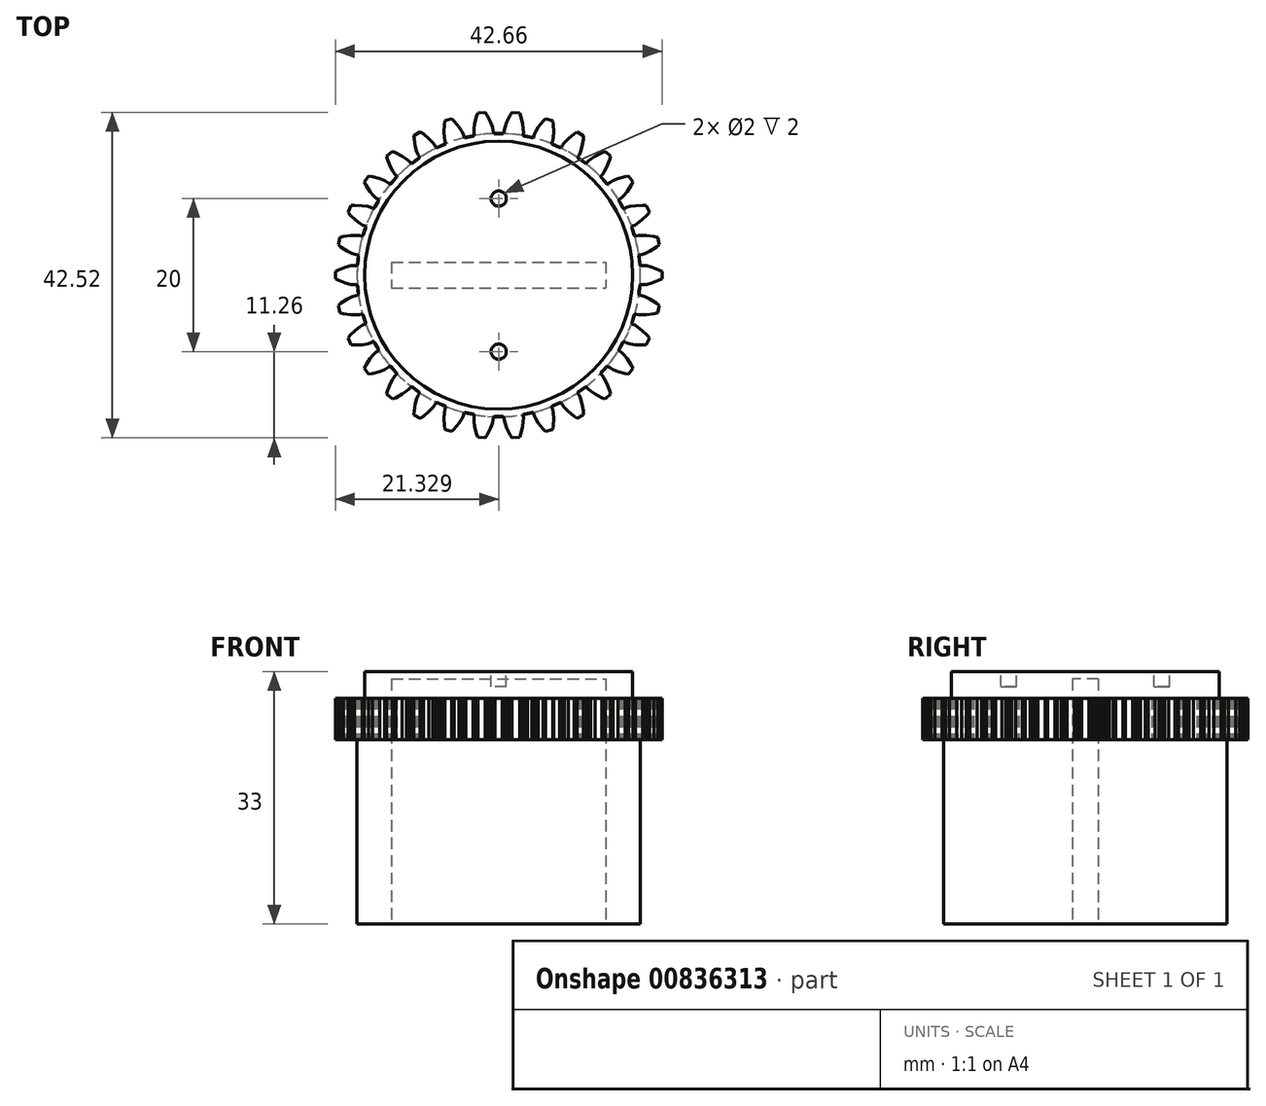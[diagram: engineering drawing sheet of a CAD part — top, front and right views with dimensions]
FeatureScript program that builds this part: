
annotation { "Feature Type Name" : "Feature", "Feature Type Description" : "" }
export const myFeature = defineFeature(function(context is Context, id is Id, definition is map)
    precondition{}
    {
        {
            var Q0;
            Q0=qCreatedBy(makeId("Top.planeOp"),FACE);
            var sketch = newSketch(context, id + "F0", { "sketchPlane" : qUnion([Q0])});
            skLineSegment(sketch, "E0", {"start": v(5.95, 16.64) * mm, "end": v(6.04, 16.7) * mm});
            skLineSegment(sketch, "E1", {"start": v(6.04, 16.7) * mm, "end": v(6.12, 16.74) * mm});
            skLineSegment(sketch, "E2", {"start": v(21.02, -17.09) * mm, "end": v(21.05, -17.07) * mm});
            skLineSegment(sketch, "E3", {"start": v(32.31, -2.53) * mm, "end": v(32.33, -2.41) * mm});
            skLineSegment(sketch, "E4", {"start": v(32.33, -2.41) * mm, "end": v(32.35, -2.32) * mm});
            skLineSegment(sketch, "E5", {"start": v(6.12, 16.74) * mm, "end": v(6.43, 16.86) * mm});
            skLineSegment(sketch, "E6", {"start": v(6.43, 16.86) * mm, "end": v(6.95, 17.06) * mm});
            skLineSegment(sketch, "E7", {"start": v(6.13, -16.74) * mm, "end": v(6.43, -16.86) * mm});
            skLineSegment(sketch, "E8", {"start": v(6.43, -16.86) * mm, "end": v(6.95, -17.06) * mm});
            skLineSegment(sketch, "E9", {"start": v(17.47, -18.17) * mm, "end": v(17.79, -18.09) * mm});
            skLineSegment(sketch, "E10", {"start": v(17.79, -18.09) * mm, "end": v(18.32, -17.95) * mm});
            skLineSegment(sketch, "E11", {"start": v(21.86, -16.75) * mm, "end": v(21.96, -16.7) * mm});
            skLineSegment(sketch, "E12", {"start": v(21.96, -16.7) * mm, "end": v(22.05, -16.64) * mm});
            skLineSegment(sketch, "E13", {"start": v(10.18, 18.1) * mm, "end": v(10.52, 18.17) * mm});
            skLineSegment(sketch, "E14", {"start": v(-4.35, 2.32) * mm, "end": v(-4.34, 2.41) * mm});
            skLineSegment(sketch, "E15", {"start": v(-4.34, 2.41) * mm, "end": v(-4.31, 2.53) * mm});
            skLineSegment(sketch, "E16", {"start": v(10.53, -18.17) * mm, "end": v(10.63, -18.18) * mm});
            skLineSegment(sketch, "E17", {"start": v(10.63, -18.18) * mm, "end": v(10.73, -18.2) * mm});
            skLineSegment(sketch, "E18", {"start": v(32.37, 1.98) * mm, "end": v(32.35, 2.27) * mm});
            skLineSegment(sketch, "E19", {"start": v(10.18, -18.1) * mm, "end": v(10.53, -18.17) * mm});
            skLineSegment(sketch, "E20", {"start": v(27.49, -12.66) * mm, "end": v(27.7, -12.4) * mm});
            skLineSegment(sketch, "E21", {"start": v(27.7, -12.4) * mm, "end": v(28.05, -11.98) * mm});
            skLineSegment(sketch, "E22", {"start": v(21.02, 17.09) * mm, "end": v(21.05, 17.07) * mm});
            skLineSegment(sketch, "E23", {"start": v(32.35, -2.27) * mm, "end": v(32.37, -1.98) * mm});
            skLineSegment(sketch, "E24", {"start": v(32.33, 2.41) * mm, "end": v(32.31, 2.52) * mm});
            skLineSegment(sketch, "E25", {"start": v(17.26, 18.2) * mm, "end": v(17.37, 18.18) * mm});
            skLineSegment(sketch, "E26", {"start": v(17.47, 18.17) * mm, "end": v(17.79, 18.09) * mm});
            skLineSegment(sketch, "E27", {"start": v(17.79, 18.09) * mm, "end": v(18.32, 17.95) * mm});
            skLineSegment(sketch, "E28", {"start": v(19.8, -20.1) * mm, "end": v(20.12, -20.44) * mm});
            skLineSegment(sketch, "E29", {"start": v(22.35, -17) * mm, "end": v(22.6, -17.33) * mm});
            skLineSegment(sketch, "E30", {"start": v(28.5, -15.07) * mm, "end": v(28.64, -15.52) * mm});
            skLineSegment(sketch, "E31", {"start": v(5.65, -17) * mm, "end": v(5.77, -16.76) * mm});
            skLineSegment(sketch, "E32", {"start": v(27.4, -13) * mm, "end": v(27.58, -13.2) * mm});
            skLineSegment(sketch, "E33", {"start": v(17.23, 18.66) * mm, "end": v(17.22, 19.08) * mm});
            skLineSegment(sketch, "E34", {"start": v(28.64, -15.52) * mm, "end": v(27.9, -16.18) * mm});
            skLineSegment(sketch, "E35", {"start": v(27.34, -12.9) * mm, "end": v(27.4, -13) * mm});
            skLineSegment(sketch, "E36", {"start": v(27.47, -16) * mm, "end": v(26.6, -15.55) * mm});
            skLineSegment(sketch, "E37", {"start": v(26.02, -15.16) * mm, "end": v(25.7, -14.88) * mm});
            skLineSegment(sketch, "E38", {"start": v(10.8, -18.28) * mm, "end": v(10.8, -18.4) * mm});
            skLineSegment(sketch, "E39", {"start": v(27.9, -16.18) * mm, "end": v(27.47, -16) * mm});
            skLineSegment(sketch, "E40", {"start": v(26.6, -15.55) * mm, "end": v(26.02, -15.16) * mm});
            skLineSegment(sketch, "E41", {"start": v(10.73, -18.2) * mm, "end": v(10.8, -18.28) * mm});
            skLineSegment(sketch, "E42", {"start": v(10.73, -18.2) * mm, "end": v(10.63, -18.15) * mm});
            skLineSegment(sketch, "E43", {"start": v(13.41, -18.48) * mm, "end": v(13.33, -18.55) * mm});
            skLineSegment(sketch, "E44", {"start": v(30.5, -8.72) * mm, "end": v(30.4, -8.7) * mm});
            skLineSegment(sketch, "E45", {"start": v(18.56, -18.1) * mm, "end": v(18.64, -18.36) * mm});
            skLineSegment(sketch, "E46", {"start": v(24.7, -16.12) * mm, "end": v(24.9, -16.8) * mm});
            skLineSegment(sketch, "E47", {"start": v(-5.77, -3.14) * mm, "end": v(-5.14, -2.83) * mm});
            skLineSegment(sketch, "E48", {"start": v(34.3, -5.02) * mm, "end": v(33.33, -5.17) * mm});
            skLineSegment(sketch, "E49", {"start": v(12.95, 19.99) * mm, "end": v(13.18, 19.33) * mm});
            skLineSegment(sketch, "E50", {"start": v(12.26, 21.26) * mm, "end": v(12.5, 20.86) * mm});
            skLineSegment(sketch, "E51", {"start": v(12.5, 20.86) * mm, "end": v(12.95, 19.99) * mm});
            skLineSegment(sketch, "E52", {"start": v(33.33, -5.17) * mm, "end": v(32.63, -5.2) * mm});
            skLineSegment(sketch, "E53", {"start": v(32.63, -5.2) * mm, "end": v(32.22, -5.16) * mm});
            skLineSegment(sketch, "E54", {"start": v(28.9, -12.33) * mm, "end": v(28.54, -12.12) * mm});
            skLineSegment(sketch, "E55", {"start": v(13.28, 18.92) * mm, "end": v(13.18, 19.33) * mm});
            skLineSegment(sketch, "E56", {"start": v(0.6, -12.7) * mm, "end": v(0.66, -12.8) * mm});
            skLineSegment(sketch, "E57", {"start": v(15.5, -20.86) * mm, "end": v(15.74, -21.26) * mm});
            skLineSegment(sketch, "E58", {"start": v(16.72, -21.16) * mm, "end": v(15.74, -21.26) * mm});
            skLineSegment(sketch, "E59", {"start": v(15.05, -19.99) * mm, "end": v(15.5, -20.86) * mm});
            skLineSegment(sketch, "E60", {"start": v(28.33, -11.96) * mm, "end": v(28.23, -11.92) * mm});
            skLineSegment(sketch, "E61", {"start": v(27.82, 13.54) * mm, "end": v(27.58, 13.2) * mm});
            skLineSegment(sketch, "E62", {"start": v(28.54, -12.12) * mm, "end": v(28.33, -11.96) * mm});
            skLineSegment(sketch, "E63", {"start": v(9.44, 18.1) * mm, "end": v(9.36, 18.36) * mm});
            skLineSegment(sketch, "E64", {"start": v(10.78, 19.08) * mm, "end": v(10.77, 18.66) * mm});
            skLineSegment(sketch, "E65", {"start": v(10.8, -18.4) * mm, "end": v(10.77, -18.66) * mm});
            skLineSegment(sketch, "E66", {"start": v(-4.3, -2.4) * mm, "end": v(-4.31, -2.52) * mm});
            skLineSegment(sketch, "E67", {"start": v(17.47, -18.17) * mm, "end": v(17.26, -18.2) * mm});
            skLineSegment(sketch, "E68", {"start": v(-4.36, -2.32) * mm, "end": v(-4.31, -2.52) * mm});
            skLineSegment(sketch, "E69", {"start": v(21.86, 16.75) * mm, "end": v(22.05, 16.64) * mm});
            skLineSegment(sketch, "E70", {"start": v(-4.36, -2.32) * mm, "end": v(-4.44, -1.35) * mm});
            skLineSegment(sketch, "E71", {"start": v(0.51, -12.66) * mm, "end": v(-0.12, -11.93) * mm});
            skLineSegment(sketch, "E72", {"start": v(30.21, -8.91) * mm, "end": v(29.7, -9.75) * mm});
            skLineSegment(sketch, "E73", {"start": v(30.5, 1.75) * mm, "end": v(30.5, -1.75) * mm, "construction": true});
            skLineSegment(sketch, "E74", {"start": v(27.48, 12.66) * mm, "end": v(27.34, 12.8) * mm});
            skLineSegment(sketch, "E75", {"start": v(0.51, 12.66) * mm, "end": v(0.66, 12.8) * mm});
            skLineSegment(sketch, "E76", {"start": v(27.49, -12.66) * mm, "end": v(27.34, -12.8) * mm});
            skLineSegment(sketch, "E77", {"start": v(-2.5, -1.75) * mm, "end": v(-2.5, 1.75) * mm, "construction": true});
            skLineSegment(sketch, "E78", {"start": v(-2.21, 8.9) * mm, "end": v(-1.7, 9.75) * mm});
            skLineSegment(sketch, "E79", {"start": v(0.51, -12.66) * mm, "end": v(0.66, -12.8) * mm});
            skLineSegment(sketch, "E80", {"start": v(30.21, 8.9) * mm, "end": v(29.74, 9.64) * mm});
            skLineSegment(sketch, "E81", {"start": v(30.21, -8.91) * mm, "end": v(30.3, -8.73) * mm});
            skLineSegment(sketch, "E82", {"start": v(10.52, 18.17) * mm, "end": v(10.73, 18.2) * mm});
            skLineSegment(sketch, "E83", {"start": v(17.23, -18.66) * mm, "end": v(17.2, -18.4) * mm});
            skLineSegment(sketch, "E84", {"start": v(-3.54, -12.14) * mm, "end": v(-3.32, -11.73) * mm});
            skLineSegment(sketch, "E85", {"start": v(30.4, 8.7) * mm, "end": v(30.5, 8.72) * mm});
            skLineSegment(sketch, "E86", {"start": v(-2.97, -12.93) * mm, "end": v(-3.54, -12.14) * mm});
            skLineSegment(sketch, "E87", {"start": v(-5.68, 8.23) * mm, "end": v(-5.38, 7.87) * mm});
            skLineSegment(sketch, "E88", {"start": v(21.12, 19.67) * mm, "end": v(21.17, 18.69) * mm});
            skLineSegment(sketch, "E89", {"start": v(9.36, 18.36) * mm, "end": v(9.18, 18.74) * mm});
            skLineSegment(sketch, "E90", {"start": v(-4.69, 7.18) * mm, "end": v(-5.38, 7.87) * mm});
            skLineSegment(sketch, "E91", {"start": v(31.85, 5.1) * mm, "end": v(31.96, 5.1) * mm});
            skLineSegment(sketch, "E92", {"start": v(-2.97, 12.93) * mm, "end": v(-2.5, 12.85) * mm});
            skLineSegment(sketch, "E93", {"start": v(28.23, -11.92) * mm, "end": v(28.12, -11.93) * mm});
            skLineSegment(sketch, "E94", {"start": v(34.6, 3.67) * mm, "end": v(33.77, 3.14) * mm});
            skLineSegment(sketch, "E95", {"start": v(31.39, -6.27) * mm, "end": v(31.43, -6.37) * mm});
            skLineSegment(sketch, "E96", {"start": v(12.95, -19.99) * mm, "end": v(12.5, -20.86) * mm});
            skLineSegment(sketch, "E97", {"start": v(10.63, 18.15) * mm, "end": v(10.73, 18.2) * mm});
            skLineSegment(sketch, "E98", {"start": v(3.3, 16.12) * mm, "end": v(3.46, 15.73) * mm});
            skLineSegment(sketch, "E99", {"start": v(21.12, 18) * mm, "end": v(21.04, 17.58) * mm});
            skLineSegment(sketch, "E100", {"start": v(34.96, 3.95) * mm, "end": v(34.6, 3.67) * mm});
            skLineSegment(sketch, "E101", {"start": v(-4.31, 2.53) * mm, "end": v(-4.3, 2.4) * mm});
            skLineSegment(sketch, "E102", {"start": v(20.95, -17.33) * mm, "end": v(20.93, -17.22) * mm});
            skLineSegment(sketch, "E103", {"start": v(24.4, -15.5) * mm, "end": v(24.36, -15.4) * mm});
            skLineSegment(sketch, "E104", {"start": v(9.36, -18.36) * mm, "end": v(9.44, -18.1) * mm});
            skLineSegment(sketch, "E105", {"start": v(13.28, -18.92) * mm, "end": v(13.3, -18.65) * mm});
            skLineSegment(sketch, "E106", {"start": v(17.2, -18.4) * mm, "end": v(17.2, -18.28) * mm});
            skLineSegment(sketch, "E107", {"start": v(27.39, 12.7) * mm, "end": v(27.34, 12.8) * mm});
            skLineSegment(sketch, "E108", {"start": v(5.65, 17) * mm, "end": v(5.4, 17.33) * mm});
            skLineSegment(sketch, "E109", {"start": v(17.2, 18.28) * mm, "end": v(17.2, 18.4) * mm});
            skLineSegment(sketch, "E110", {"start": v(10.7, 17.33) * mm, "end": v(8.55, 16.78) * mm});
            skLineSegment(sketch, "E111", {"start": v(17.3, 17.33) * mm, "end": v(15.1, 17.6) * mm});
            skLineSegment(sketch, "E112", {"start": v(8.55, 16.78) * mm, "end": v(6.49, 15.96) * mm});
            skLineSegment(sketch, "E113", {"start": v(15.1, 17.6) * mm, "end": v(12.9, 17.6) * mm});
            skLineSegment(sketch, "E114", {"start": v(19.45, 16.78) * mm, "end": v(17.3, 17.33) * mm});
            skLineSegment(sketch, "E115", {"start": v(12.9, 17.6) * mm, "end": v(10.7, 17.33) * mm});
            skLineSegment(sketch, "E116", {"start": v(23.1, 17.83) * mm, "end": v(22.6, 17.33) * mm});
            skLineSegment(sketch, "E117", {"start": v(20.93, 17.22) * mm, "end": v(20.95, 17.33) * mm});
            skLineSegment(sketch, "E118", {"start": v(30.5, 1.75) * mm, "end": v(-2.5, 1.75) * mm, "construction": true});
            skLineSegment(sketch, "E119", {"start": v(22.05, 16.64) * mm, "end": v(21.94, 16.66) * mm});
            skLineSegment(sketch, "E120", {"start": v(22.6, 17.33) * mm, "end": v(22.35, 17) * mm});
            skLineSegment(sketch, "E121", {"start": v(-2.5, -1.75) * mm, "end": v(30.5, -1.75) * mm, "construction": true});
            skLineSegment(sketch, "E122", {"start": v(21.94, 16.66) * mm, "end": v(21.05, 17.07) * mm});
            skLineSegment(sketch, "E123", {"start": v(22.15, 16.67) * mm, "end": v(22.05, 16.64) * mm});
            skLineSegment(sketch, "E124", {"start": v(22.22, 16.76) * mm, "end": v(22.15, 16.67) * mm});
            skLineSegment(sketch, "E125", {"start": v(22.35, 17) * mm, "end": v(22.22, 16.76) * mm});
            skLineSegment(sketch, "E126", {"start": v(20.98, 17.12) * mm, "end": v(20.93, 17.22) * mm});
            skLineSegment(sketch, "E127", {"start": v(23.85, 18.45) * mm, "end": v(23.1, 17.83) * mm});
            skLineSegment(sketch, "E128", {"start": v(24.24, 18.72) * mm, "end": v(23.85, 18.45) * mm});
            skLineSegment(sketch, "E129", {"start": v(26.02, 15.16) * mm, "end": v(25.7, 14.88) * mm});
            skLineSegment(sketch, "E130", {"start": v(26.6, 15.55) * mm, "end": v(26.02, 15.16) * mm});
            skLineSegment(sketch, "E131", {"start": v(24.38, 15.3) * mm, "end": v(24.36, 15.4) * mm});
            skLineSegment(sketch, "E132", {"start": v(25.05, 17.76) * mm, "end": v(25.09, 18.22) * mm});
            skLineSegment(sketch, "E133", {"start": v(24.54, 15.73) * mm, "end": v(24.7, 16.12) * mm});
            skLineSegment(sketch, "E134", {"start": v(24.36, 15.4) * mm, "end": v(24.4, 15.5) * mm});
            skLineSegment(sketch, "E135", {"start": v(24.4, 15.5) * mm, "end": v(24.54, 15.73) * mm});
            skLineSegment(sketch, "E136", {"start": v(24.9, 16.8) * mm, "end": v(25.05, 17.76) * mm});
            skLineSegment(sketch, "E137", {"start": v(25.23, 14.64) * mm, "end": v(24.46, 15.21) * mm});
            skLineSegment(sketch, "E138", {"start": v(25.09, 18.22) * mm, "end": v(24.24, 18.72) * mm});
            skLineSegment(sketch, "E139", {"start": v(24.7, 16.12) * mm, "end": v(24.9, 16.8) * mm});
            skLineSegment(sketch, "E140", {"start": v(25.44, 14.62) * mm, "end": v(25.33, 14.6) * mm});
            skLineSegment(sketch, "E141", {"start": v(25.53, 14.68) * mm, "end": v(25.44, 14.62) * mm});
            skLineSegment(sketch, "E142", {"start": v(25.7, 14.88) * mm, "end": v(25.53, 14.68) * mm});
            skLineSegment(sketch, "E143", {"start": v(-2.33, -10.37) * mm, "end": v(-2.78, -10.9) * mm});
            skLineSegment(sketch, "E144", {"start": v(21.12, 19.67) * mm, "end": v(21.06, 20.13) * mm});
            skLineSegment(sketch, "E145", {"start": v(-2.03, -10.08) * mm, "end": v(-2.33, -10.37) * mm});
            skLineSegment(sketch, "E146", {"start": v(20.95, 17.33) * mm, "end": v(21.04, 17.58) * mm});
            skLineSegment(sketch, "E147", {"start": v(3.64, -15.4) * mm, "end": v(3.6, -15.5) * mm});
            skLineSegment(sketch, "E148", {"start": v(13.18, -19.33) * mm, "end": v(13.28, -18.92) * mm});
            skLineSegment(sketch, "E149", {"start": v(27.47, 16) * mm, "end": v(26.6, 15.55) * mm});
            skLineSegment(sketch, "E150", {"start": v(6.95, -17.06) * mm, "end": v(7.02, -17.12) * mm});
            skLineSegment(sketch, "E151", {"start": v(32.68, -7.18) * mm, "end": v(32.13, -6.75) * mm});
            skLineSegment(sketch, "E152", {"start": v(19.8, 20.1) * mm, "end": v(19.19, 19.33) * mm});
            skLineSegment(sketch, "E153", {"start": v(20.12, 20.44) * mm, "end": v(19.8, 20.1) * mm});
            skLineSegment(sketch, "E154", {"start": v(32.13, -6.75) * mm, "end": v(31.77, -6.53) * mm});
            skLineSegment(sketch, "E155", {"start": v(21.06, 20.13) * mm, "end": v(20.12, 20.44) * mm});
            skLineSegment(sketch, "E156", {"start": v(21.12, 18) * mm, "end": v(21.17, 18.69) * mm});
            skLineSegment(sketch, "E157", {"start": v(13.3, -18.65) * mm, "end": v(13.33, -18.55) * mm});
            skLineSegment(sketch, "E158", {"start": v(21.94, -16.66) * mm, "end": v(22.05, -16.64) * mm});
            skLineSegment(sketch, "E159", {"start": v(-1.8, -9.93) * mm, "end": v(-2.03, -10.08) * mm});
            skLineSegment(sketch, "E160", {"start": v(18.64, 18.36) * mm, "end": v(18.56, 18.1) * mm});
            skLineSegment(sketch, "E161", {"start": v(22.05, -16.64) * mm, "end": v(22.15, -16.67) * mm});
            skLineSegment(sketch, "E162", {"start": v(18.82, 18.74) * mm, "end": v(18.64, 18.36) * mm});
            skLineSegment(sketch, "E163", {"start": v(7.02, -17.12) * mm, "end": v(7.06, -17.22) * mm});
            skLineSegment(sketch, "E164", {"start": v(17.36, 18.15) * mm, "end": v(17.26, 18.2) * mm});
            skLineSegment(sketch, "E165", {"start": v(17.2, -18.28) * mm, "end": v(17.26, -18.2) * mm});
            skLineSegment(sketch, "E166", {"start": v(19.19, 19.33) * mm, "end": v(18.82, 18.74) * mm});
            skLineSegment(sketch, "E167", {"start": v(18.42, 17.95) * mm, "end": v(18.32, 17.95) * mm});
            skLineSegment(sketch, "E168", {"start": v(18.5, 18) * mm, "end": v(18.42, 17.95) * mm});
            skLineSegment(sketch, "E169", {"start": v(18.56, 18.1) * mm, "end": v(18.5, 18) * mm});
            skLineSegment(sketch, "E170", {"start": v(22.15, -16.67) * mm, "end": v(22.22, -16.76) * mm});
            skLineSegment(sketch, "E171", {"start": v(33.38, -7.87) * mm, "end": v(32.68, -7.18) * mm});
            skLineSegment(sketch, "E172", {"start": v(17.26, 18.2) * mm, "end": v(17.2, 18.28) * mm});
            skLineSegment(sketch, "E173", {"start": v(21.05, -17.07) * mm, "end": v(21.94, -16.66) * mm});
            skLineSegment(sketch, "E174", {"start": v(21.04, -17.58) * mm, "end": v(20.95, -17.33) * mm});
            skLineSegment(sketch, "E175", {"start": v(21.17, -18.69) * mm, "end": v(21.12, -18) * mm});
            skLineSegment(sketch, "E176", {"start": v(17.2, 18.4) * mm, "end": v(17.23, 18.66) * mm});
            skLineSegment(sketch, "E177", {"start": v(20.93, -17.22) * mm, "end": v(20.98, -17.12) * mm});
            skLineSegment(sketch, "E178", {"start": v(14.48, 18.45) * mm, "end": v(13.52, 18.45) * mm});
            skLineSegment(sketch, "E179", {"start": v(14.7, 18.65) * mm, "end": v(14.67, 18.55) * mm});
            skLineSegment(sketch, "E180", {"start": v(14.72, 18.92) * mm, "end": v(14.7, 18.65) * mm});
            skLineSegment(sketch, "E181", {"start": v(14.81, 19.33) * mm, "end": v(14.72, 18.92) * mm});
            skLineSegment(sketch, "E182", {"start": v(15.05, 19.99) * mm, "end": v(14.81, 19.33) * mm});
            skLineSegment(sketch, "E183", {"start": v(21.12, -18) * mm, "end": v(21.04, -17.58) * mm});
            skLineSegment(sketch, "E184", {"start": v(14.67, 18.55) * mm, "end": v(14.59, 18.48) * mm});
            skLineSegment(sketch, "E185", {"start": v(25.09, -18.22) * mm, "end": v(25.05, -17.76) * mm});
            skLineSegment(sketch, "E186", {"start": v(16.87, 20.72) * mm, "end": v(16.72, 21.16) * mm});
            skLineSegment(sketch, "E187", {"start": v(13.3, 18.65) * mm, "end": v(13.28, 18.92) * mm});
            skLineSegment(sketch, "E188", {"start": v(31.75, -5.15) * mm, "end": v(31.85, -5.1) * mm});
            skLineSegment(sketch, "E189", {"start": v(11.12, 20.72) * mm, "end": v(10.87, 19.77) * mm});
            skLineSegment(sketch, "E190", {"start": v(12.26, 21.26) * mm, "end": v(11.28, 21.16) * mm});
            skLineSegment(sketch, "E191", {"start": v(10.87, 19.77) * mm, "end": v(10.78, 19.08) * mm});
            skLineSegment(sketch, "E192", {"start": v(33.68, -8.23) * mm, "end": v(33.38, -7.87) * mm});
            skLineSegment(sketch, "E193", {"start": v(15.74, 21.26) * mm, "end": v(15.5, 20.86) * mm});
            skLineSegment(sketch, "E194", {"start": v(17.12, 19.77) * mm, "end": v(16.87, 20.72) * mm});
            skLineSegment(sketch, "E195", {"start": v(11.28, 21.16) * mm, "end": v(11.12, 20.72) * mm});
            skLineSegment(sketch, "E196", {"start": v(15.5, 20.86) * mm, "end": v(15.05, 19.99) * mm});
            skLineSegment(sketch, "E197", {"start": v(13.33, 18.55) * mm, "end": v(13.3, 18.65) * mm});
            skLineSegment(sketch, "E198", {"start": v(16.72, 21.16) * mm, "end": v(15.74, 21.26) * mm});
            skLineSegment(sketch, "E199", {"start": v(11.28, -21.16) * mm, "end": v(12.26, -21.26) * mm});
            skLineSegment(sketch, "E200", {"start": v(27.34, -12.8) * mm, "end": v(27.39, -12.7) * mm});
            skLineSegment(sketch, "E201", {"start": v(10.8, 18.28) * mm, "end": v(10.73, 18.2) * mm});
            skLineSegment(sketch, "E202", {"start": v(10.8, 18.4) * mm, "end": v(10.8, 18.28) * mm});
            skLineSegment(sketch, "E203", {"start": v(11.12, -20.72) * mm, "end": v(11.28, -21.16) * mm});
            skLineSegment(sketch, "E204", {"start": v(10.77, 18.66) * mm, "end": v(10.8, 18.4) * mm});
            skLineSegment(sketch, "E205", {"start": v(3.6, -15.5) * mm, "end": v(3.46, -15.73) * mm});
            skLineSegment(sketch, "E206", {"start": v(-6.9, -0.7) * mm, "end": v(-6, -1.04) * mm});
            skLineSegment(sketch, "E207", {"start": v(-6.9, 0.7) * mm, "end": v(-7.33, 0.5) * mm});
            skLineSegment(sketch, "E208", {"start": v(10.87, -19.77) * mm, "end": v(11.12, -20.72) * mm});
            skLineSegment(sketch, "E209", {"start": v(10.78, -19.08) * mm, "end": v(10.87, -19.77) * mm});
            skLineSegment(sketch, "E210", {"start": v(12.26, -21.26) * mm, "end": v(12.5, -20.86) * mm});
            skLineSegment(sketch, "E211", {"start": v(-7.33, -0.5) * mm, "end": v(-6.9, -0.7) * mm});
            skLineSegment(sketch, "E212", {"start": v(23.85, -18.45) * mm, "end": v(24.24, -18.72) * mm});
            skLineSegment(sketch, "E213", {"start": v(9.58, 17.95) * mm, "end": v(9.49, 18) * mm});
            skLineSegment(sketch, "E214", {"start": v(-7.33, 0.5) * mm, "end": v(-7.33, -0.5) * mm});
            skLineSegment(sketch, "E215", {"start": v(-4.22, -5.16) * mm, "end": v(-3.96, -5.1) * mm});
            skLineSegment(sketch, "E216", {"start": v(3.46, -15.73) * mm, "end": v(3.3, -16.12) * mm});
            skLineSegment(sketch, "E217", {"start": v(-3.7, -5.24) * mm, "end": v(-3.4, -6.16) * mm});
            skLineSegment(sketch, "E218", {"start": v(-5.38, -7.87) * mm, "end": v(-5.68, -8.23) * mm});
            skLineSegment(sketch, "E219", {"start": v(9.49, 18) * mm, "end": v(9.44, 18.1) * mm});
            skLineSegment(sketch, "E220", {"start": v(-3.85, -5.1) * mm, "end": v(-3.75, -5.15) * mm});
            skLineSegment(sketch, "E221", {"start": v(-5.3, 1.2) * mm, "end": v(-6, 1.04) * mm});
            skLineSegment(sketch, "E222", {"start": v(-6, 1.04) * mm, "end": v(-6.9, 0.7) * mm});
            skLineSegment(sketch, "E223", {"start": v(8.81, 19.33) * mm, "end": v(8.2, 20.1) * mm});
            skLineSegment(sketch, "E224", {"start": v(3.3, -16.12) * mm, "end": v(3.1, -16.8) * mm});
            skLineSegment(sketch, "E225", {"start": v(9.18, 18.74) * mm, "end": v(8.81, 19.33) * mm});
            skLineSegment(sketch, "E226", {"start": v(-5.68, -8.23) * mm, "end": v(-5.28, -9.12) * mm});
            skLineSegment(sketch, "E227", {"start": v(-3.96, -5.1) * mm, "end": v(-3.85, -5.1) * mm});
            skLineSegment(sketch, "E228", {"start": v(7.88, 20.44) * mm, "end": v(6.94, 20.13) * mm});
            skLineSegment(sketch, "E229", {"start": v(-4.31, -2.52) * mm, "end": v(-4.38, -2.6) * mm});
            skLineSegment(sketch, "E230", {"start": v(-4.4, 1.45) * mm, "end": v(-4.44, 1.35) * mm});
            skLineSegment(sketch, "E231", {"start": v(-4.74, -2.7) * mm, "end": v(-5.14, -2.83) * mm});
            skLineSegment(sketch, "E232", {"start": v(2.95, 17.76) * mm, "end": v(3.1, 16.8) * mm});
            skLineSegment(sketch, "E233", {"start": v(5.95, -16.64) * mm, "end": v(6.05, -16.66) * mm});
            skLineSegment(sketch, "E234", {"start": v(-4.48, -2.65) * mm, "end": v(-4.74, -2.7) * mm});
            skLineSegment(sketch, "E235", {"start": v(-4.38, -2.6) * mm, "end": v(-4.48, -2.65) * mm});
            skLineSegment(sketch, "E236", {"start": v(-4.44, 1.35) * mm, "end": v(-4.52, 1.28) * mm});
            skLineSegment(sketch, "E237", {"start": v(-5.14, 2.83) * mm, "end": v(-4.74, 2.7) * mm});
            skLineSegment(sketch, "E238", {"start": v(-4.52, 1.28) * mm, "end": v(-4.63, 1.25) * mm});
            skLineSegment(sketch, "E239", {"start": v(-6, -1.04) * mm, "end": v(-5.3, -1.2) * mm});
            skLineSegment(sketch, "E240", {"start": v(14.59, -18.48) * mm, "end": v(14.67, -18.55) * mm});
            skLineSegment(sketch, "E241", {"start": v(30.22, -8.8) * mm, "end": v(30.3, -8.73) * mm});
            skLineSegment(sketch, "E242", {"start": v(2.95, -17.76) * mm, "end": v(2.9, -18.22) * mm});
            skLineSegment(sketch, "E243", {"start": v(29.7, -9.75) * mm, "end": v(29.74, -9.64) * mm});
            skLineSegment(sketch, "E244", {"start": v(3.1, -16.8) * mm, "end": v(2.95, -17.76) * mm});
            skLineSegment(sketch, "E245", {"start": v(5.77, -16.76) * mm, "end": v(5.84, -16.67) * mm});
            skLineSegment(sketch, "E246", {"start": v(8.2, 20.1) * mm, "end": v(7.88, 20.44) * mm});
            skLineSegment(sketch, "E247", {"start": v(3.54, 15.21) * mm, "end": v(2.76, 14.64) * mm});
            skLineSegment(sketch, "E248", {"start": v(3.64, 15.4) * mm, "end": v(3.61, 15.3) * mm});
            skLineSegment(sketch, "E249", {"start": v(3.6, 15.5) * mm, "end": v(3.64, 15.4) * mm});
            skLineSegment(sketch, "E250", {"start": v(-5.3, -1.2) * mm, "end": v(-4.9, -1.26) * mm});
            skLineSegment(sketch, "E251", {"start": v(30.3, -8.73) * mm, "end": v(30.4, -8.7) * mm});
            skLineSegment(sketch, "E252", {"start": v(29.74, -9.64) * mm, "end": v(30.22, -8.8) * mm});
            skLineSegment(sketch, "E253", {"start": v(3.76, 18.72) * mm, "end": v(2.9, 18.22) * mm});
            skLineSegment(sketch, "E254", {"start": v(6.88, 19.67) * mm, "end": v(6.83, 18.69) * mm});
            skLineSegment(sketch, "E255", {"start": v(-5.34, -5.17) * mm, "end": v(-4.64, -5.2) * mm});
            skLineSegment(sketch, "E256", {"start": v(4.15, 18.45) * mm, "end": v(3.76, 18.72) * mm});
            skLineSegment(sketch, "E257", {"start": v(18.5, -18) * mm, "end": v(18.56, -18.1) * mm});
            skLineSegment(sketch, "E258", {"start": v(18.42, -17.95) * mm, "end": v(18.5, -18) * mm});
            skLineSegment(sketch, "E259", {"start": v(-6.76, -4.92) * mm, "end": v(-6.3, -5.02) * mm});
            skLineSegment(sketch, "E260", {"start": v(3.46, 15.73) * mm, "end": v(3.6, 15.5) * mm});
            skLineSegment(sketch, "E261", {"start": v(2.9, 18.22) * mm, "end": v(2.95, 17.76) * mm});
            skLineSegment(sketch, "E262", {"start": v(4.9, 17.83) * mm, "end": v(4.15, 18.45) * mm});
            skLineSegment(sketch, "E263", {"start": v(17.26, -18.2) * mm, "end": v(17.36, -18.15) * mm});
            skLineSegment(sketch, "E264", {"start": v(-4.64, -5.2) * mm, "end": v(-4.22, -5.16) * mm});
            skLineSegment(sketch, "E265", {"start": v(-6.3, -5.02) * mm, "end": v(-5.34, -5.17) * mm});
            skLineSegment(sketch, "E266", {"start": v(18.32, -17.95) * mm, "end": v(18.42, -17.95) * mm});
            skLineSegment(sketch, "E267", {"start": v(3.1, 16.8) * mm, "end": v(3.3, 16.12) * mm});
            skLineSegment(sketch, "E268", {"start": v(6.94, 20.13) * mm, "end": v(6.88, 19.67) * mm});
            skLineSegment(sketch, "E269", {"start": v(-0.04, 11.99) * mm, "end": v(-0.12, 11.93) * mm});
            skLineSegment(sketch, "E270", {"start": v(0.66, 12.8) * mm, "end": v(0.6, 12.7) * mm});
            skLineSegment(sketch, "E271", {"start": v(-4.63, -1.25) * mm, "end": v(-4.52, -1.28) * mm});
            skLineSegment(sketch, "E272", {"start": v(0.66, 12.9) * mm, "end": v(0.66, 12.8) * mm});
            skLineSegment(sketch, "E273", {"start": v(-4.9, -1.26) * mm, "end": v(-4.63, -1.25) * mm});
            skLineSegment(sketch, "E274", {"start": v(-2.97, 12.93) * mm, "end": v(-3.54, 12.14) * mm});
            skLineSegment(sketch, "E275", {"start": v(-0.23, 11.92) * mm, "end": v(-0.33, 11.96) * mm});
            skLineSegment(sketch, "E276", {"start": v(-3.54, 12.14) * mm, "end": v(-3.32, 11.73) * mm});
            skLineSegment(sketch, "E277", {"start": v(2.66, 14.6) * mm, "end": v(2.56, 14.62) * mm});
            skLineSegment(sketch, "E278", {"start": v(-4.69, -7.18) * mm, "end": v(-5.38, -7.87) * mm});
            skLineSegment(sketch, "E279", {"start": v(-0.12, 11.93) * mm, "end": v(-0.23, 11.92) * mm});
            skLineSegment(sketch, "E280", {"start": v(-4.52, -1.28) * mm, "end": v(-4.44, -1.35) * mm});
            skLineSegment(sketch, "E281", {"start": v(5.84, 16.67) * mm, "end": v(5.77, 16.76) * mm});
            skLineSegment(sketch, "E282", {"start": v(-2.3, 8.73) * mm, "end": v(-2.4, 8.7) * mm});
            skLineSegment(sketch, "E283", {"start": v(-1.73, 9.85) * mm, "end": v(-1.7, 9.75) * mm});
            skLineSegment(sketch, "E284", {"start": v(-3.84, 9.08) * mm, "end": v(-4.82, 9.14) * mm});
            skLineSegment(sketch, "E285", {"start": v(6.05, 16.66) * mm, "end": v(5.95, 16.64) * mm});
            skLineSegment(sketch, "E286", {"start": v(-2.22, 8.8) * mm, "end": v(-2.3, 8.73) * mm});
            skLineSegment(sketch, "E287", {"start": v(-1.7, 9.75) * mm, "end": v(-1.74, 9.64) * mm});
            skLineSegment(sketch, "E288", {"start": v(-1.8, 9.93) * mm, "end": v(-1.73, 9.85) * mm});
            skLineSegment(sketch, "E289", {"start": v(7.06, 17.22) * mm, "end": v(7.02, 17.12) * mm});
            skLineSegment(sketch, "E290", {"start": v(-2.5, 8.72) * mm, "end": v(-2.75, 8.84) * mm});
            skLineSegment(sketch, "E291", {"start": v(-3.15, 8.96) * mm, "end": v(-3.84, 9.08) * mm});
            skLineSegment(sketch, "E292", {"start": v(-2.75, 8.84) * mm, "end": v(-3.15, 8.96) * mm});
            skLineSegment(sketch, "E293", {"start": v(5.95, 16.64) * mm, "end": v(5.84, 16.67) * mm});
            skLineSegment(sketch, "E294", {"start": v(7.02, 17.12) * mm, "end": v(6.95, 17.06) * mm});
            skLineSegment(sketch, "E295", {"start": v(-2.4, 8.7) * mm, "end": v(-2.5, 8.72) * mm});
            skLineSegment(sketch, "E296", {"start": v(-5.77, 3.14) * mm, "end": v(-5.14, 2.83) * mm});
            skLineSegment(sketch, "E297", {"start": v(-3.32, 11.73) * mm, "end": v(-2.78, 10.9) * mm});
            skLineSegment(sketch, "E298", {"start": v(-6.3, 5.02) * mm, "end": v(-6.76, 4.92) * mm});
            skLineSegment(sketch, "E299", {"start": v(-4.38, 2.6) * mm, "end": v(-4.31, 2.53) * mm});
            skLineSegment(sketch, "E300", {"start": v(-4.64, 5.2) * mm, "end": v(-5.34, 5.17) * mm});
            skLineSegment(sketch, "E301", {"start": v(-2.03, 10.08) * mm, "end": v(-1.8, 9.93) * mm});
            skLineSegment(sketch, "E302", {"start": v(-2.78, 10.9) * mm, "end": v(-2.33, 10.37) * mm});
            skLineSegment(sketch, "E303", {"start": v(-4.63, 1.25) * mm, "end": v(-4.9, 1.26) * mm});
            skLineSegment(sketch, "E304", {"start": v(-4.74, 2.7) * mm, "end": v(-4.48, 2.65) * mm});
            skLineSegment(sketch, "E305", {"start": v(-4.82, 9.14) * mm, "end": v(-5.28, 9.12) * mm});
            skLineSegment(sketch, "E306", {"start": v(-6.96, 3.95) * mm, "end": v(-6.6, 3.67) * mm});
            skLineSegment(sketch, "E307", {"start": v(-6.76, 4.92) * mm, "end": v(-6.96, 3.95) * mm});
            skLineSegment(sketch, "E308", {"start": v(-2.33, 10.37) * mm, "end": v(-2.03, 10.08) * mm});
            skLineSegment(sketch, "E309", {"start": v(-6.6, 3.67) * mm, "end": v(-5.77, 3.14) * mm});
            skLineSegment(sketch, "E310", {"start": v(-5.34, 5.17) * mm, "end": v(-6.3, 5.02) * mm});
            skLineSegment(sketch, "E311", {"start": v(-4.48, 2.65) * mm, "end": v(-4.38, 2.6) * mm});
            skLineSegment(sketch, "E312", {"start": v(-4.13, 6.75) * mm, "end": v(-3.77, 6.53) * mm});
            skLineSegment(sketch, "E313", {"start": v(1.98, 15.16) * mm, "end": v(1.4, 15.55) * mm});
            skLineSegment(sketch, "E314", {"start": v(-3.44, 6.37) * mm, "end": v(-3.4, 6.27) * mm});
            skLineSegment(sketch, "E315", {"start": v(-3.85, 5.1) * mm, "end": v(-3.96, 5.1) * mm});
            skLineSegment(sketch, "E316", {"start": v(-3.4, 6.16) * mm, "end": v(-3.7, 5.24) * mm});
            skLineSegment(sketch, "E317", {"start": v(-3.96, 5.1) * mm, "end": v(-4.22, 5.16) * mm});
            skLineSegment(sketch, "E318", {"start": v(-3.77, 6.53) * mm, "end": v(-3.53, 6.43) * mm});
            skLineSegment(sketch, "E319", {"start": v(-3.53, 6.43) * mm, "end": v(-3.44, 6.37) * mm});
            skLineSegment(sketch, "E320", {"start": v(-4.22, 5.16) * mm, "end": v(-4.64, 5.2) * mm});
            skLineSegment(sketch, "E321", {"start": v(-4.69, 7.18) * mm, "end": v(-4.13, 6.75) * mm});
            skLineSegment(sketch, "E322", {"start": v(-3.75, 5.15) * mm, "end": v(-3.85, 5.1) * mm});
            skLineSegment(sketch, "E323", {"start": v(-0.12, -11.93) * mm, "end": v(-0.04, -11.99) * mm});
            skLineSegment(sketch, "E324", {"start": v(2.3, 14.88) * mm, "end": v(1.98, 15.16) * mm});
            skLineSegment(sketch, "E325", {"start": v(0.52, 16) * mm, "end": v(0.1, 16.18) * mm});
            skLineSegment(sketch, "E326", {"start": v(2.9, -18.22) * mm, "end": v(3.76, -18.72) * mm});
            skLineSegment(sketch, "E327", {"start": v(-0.15, 14.16) * mm, "end": v(0.18, 13.54) * mm});
            skLineSegment(sketch, "E328", {"start": v(0.42, 13.2) * mm, "end": v(0.6, 13) * mm});
            skLineSegment(sketch, "E329", {"start": v(-2.4, -8.7) * mm, "end": v(-2.3, -8.73) * mm});
            skLineSegment(sketch, "E330", {"start": v(0.6, 13) * mm, "end": v(0.66, 12.9) * mm});
            skLineSegment(sketch, "E331", {"start": v(-2.75, -8.84) * mm, "end": v(-2.5, -8.72) * mm});
            skLineSegment(sketch, "E332", {"start": v(2.47, 14.68) * mm, "end": v(2.3, 14.88) * mm});
            skLineSegment(sketch, "E333", {"start": v(-2.5, -8.72) * mm, "end": v(-2.4, -8.7) * mm});
            skLineSegment(sketch, "E334", {"start": v(0.18, 13.54) * mm, "end": v(0.42, 13.2) * mm});
            skLineSegment(sketch, "E335", {"start": v(-0.5, 15.07) * mm, "end": v(-0.15, 14.16) * mm});
            skLineSegment(sketch, "E336", {"start": v(3.76, -18.72) * mm, "end": v(4.15, -18.45) * mm});
            skLineSegment(sketch, "E337", {"start": v(-2.3, -8.73) * mm, "end": v(-2.22, -8.8) * mm});
            skLineSegment(sketch, "E338", {"start": v(-0.64, 15.52) * mm, "end": v(-0.5, 15.07) * mm});
            skLineSegment(sketch, "E339", {"start": v(7.05, 17.33) * mm, "end": v(7.06, 17.22) * mm});
            skLineSegment(sketch, "E340", {"start": v(6.96, 17.58) * mm, "end": v(7.05, 17.33) * mm});
            skLineSegment(sketch, "E341", {"start": v(7.06, -17.22) * mm, "end": v(7.05, -17.33) * mm});
            skLineSegment(sketch, "E342", {"start": v(6.83, -18.69) * mm, "end": v(6.88, -19.67) * mm});
            skLineSegment(sketch, "E343", {"start": v(6.96, -17.58) * mm, "end": v(6.88, -18) * mm});
            skLineSegment(sketch, "E344", {"start": v(6.94, -20.13) * mm, "end": v(7.88, -20.44) * mm});
            skLineSegment(sketch, "E345", {"start": v(-3.84, -9.08) * mm, "end": v(-3.15, -8.96) * mm});
            skLineSegment(sketch, "E346", {"start": v(6.88, -19.67) * mm, "end": v(6.94, -20.13) * mm});
            skLineSegment(sketch, "E347", {"start": v(34.76, -4.92) * mm, "end": v(34.96, -3.95) * mm});
            skLineSegment(sketch, "E348", {"start": v(6.88, -18) * mm, "end": v(6.83, -18.69) * mm});
            skLineSegment(sketch, "E349", {"start": v(-5.28, -9.12) * mm, "end": v(-4.82, -9.14) * mm});
            skLineSegment(sketch, "E350", {"start": v(31.85, -5.1) * mm, "end": v(31.96, -5.1) * mm});
            skLineSegment(sketch, "E351", {"start": v(-3.15, -8.96) * mm, "end": v(-2.75, -8.84) * mm});
            skLineSegment(sketch, "E352", {"start": v(7.05, -17.33) * mm, "end": v(6.96, -17.58) * mm});
            skLineSegment(sketch, "E353", {"start": v(22.6, -17.33) * mm, "end": v(23.1, -17.83) * mm});
            skLineSegment(sketch, "E354", {"start": v(23.1, -17.83) * mm, "end": v(23.85, -18.45) * mm});
            skLineSegment(sketch, "E355", {"start": v(-4.82, -9.14) * mm, "end": v(-3.84, -9.08) * mm});
            skLineSegment(sketch, "E356", {"start": v(-5.28, 9.12) * mm, "end": v(-5.68, 8.23) * mm});
            skLineSegment(sketch, "E357", {"start": v(-3.09, 4.39) * mm, "end": v(-3.5, 2.21) * mm});
            skLineSegment(sketch, "E358", {"start": v(2.75, -13.6) * mm, "end": v(4.55, -14.9) * mm});
            skLineSegment(sketch, "E359", {"start": v(4.15, -18.45) * mm, "end": v(4.9, -17.83) * mm});
            skLineSegment(sketch, "E360", {"start": v(4.9, -17.83) * mm, "end": v(5.4, -17.33) * mm});
            skLineSegment(sketch, "E361", {"start": v(31.54, -12.14) * mm, "end": v(31.32, -11.73) * mm});
            skLineSegment(sketch, "E362", {"start": v(33.28, -9.12) * mm, "end": v(33.68, -8.23) * mm});
            skLineSegment(sketch, "E363", {"start": v(31.84, -9.08) * mm, "end": v(32.82, -9.14) * mm});
            skLineSegment(sketch, "E364", {"start": v(28.05, -11.98) * mm, "end": v(28.12, -11.93) * mm});
            skLineSegment(sketch, "E365", {"start": v(-3.5, 2.21) * mm, "end": v(-3.64, 0) * mm});
            skLineSegment(sketch, "E366", {"start": v(-3.64, 0) * mm, "end": v(-3.5, -2.21) * mm});
            skLineSegment(sketch, "E367", {"start": v(-3.5, -2.21) * mm, "end": v(-3.09, -4.39) * mm});
            skLineSegment(sketch, "E368", {"start": v(31.15, -8.96) * mm, "end": v(31.84, -9.08) * mm});
            skLineSegment(sketch, "E369", {"start": v(-3.09, -4.39) * mm, "end": v(-2.4, -6.5) * mm});
            skLineSegment(sketch, "E370", {"start": v(32.82, -9.14) * mm, "end": v(33.28, -9.12) * mm});
            skLineSegment(sketch, "E371", {"start": v(-2.4, -6.5) * mm, "end": v(-1.46, -8.5) * mm});
            skLineSegment(sketch, "E372", {"start": v(-0.27, -10.37) * mm, "end": v(1.14, -12.08) * mm});
            skLineSegment(sketch, "E373", {"start": v(1.14, -12.08) * mm, "end": v(2.75, -13.6) * mm});
            skLineSegment(sketch, "E374", {"start": v(31.32, -11.73) * mm, "end": v(30.78, -10.9) * mm});
            skLineSegment(sketch, "E375", {"start": v(15.1, -17.6) * mm, "end": v(17.3, -17.33) * mm});
            skLineSegment(sketch, "E376", {"start": v(21.5, -15.96) * mm, "end": v(23.45, -14.9) * mm});
            skLineSegment(sketch, "E377", {"start": v(8.55, -16.78) * mm, "end": v(10.7, -17.33) * mm});
            skLineSegment(sketch, "E378", {"start": v(10.7, -17.33) * mm, "end": v(12.9, -17.6) * mm});
            skLineSegment(sketch, "E379", {"start": v(-1.46, 8.5) * mm, "end": v(-2.4, 6.5) * mm});
            skLineSegment(sketch, "E380", {"start": v(19.45, -16.78) * mm, "end": v(21.5, -15.96) * mm});
            skLineSegment(sketch, "E381", {"start": v(12.9, -17.6) * mm, "end": v(15.1, -17.6) * mm});
            skLineSegment(sketch, "E382", {"start": v(2.75, 13.6) * mm, "end": v(1.14, 12.08) * mm});
            skLineSegment(sketch, "E383", {"start": v(29.46, -8.5) * mm, "end": v(30.4, -6.5) * mm});
            skLineSegment(sketch, "E384", {"start": v(4.55, 14.9) * mm, "end": v(2.75, 13.6) * mm});
            skLineSegment(sketch, "E385", {"start": v(21.5, 15.96) * mm, "end": v(19.45, 16.78) * mm});
            skLineSegment(sketch, "E386", {"start": v(26.86, -12.08) * mm, "end": v(28.27, -10.37) * mm});
            skLineSegment(sketch, "E387", {"start": v(6.49, 15.96) * mm, "end": v(4.55, 14.9) * mm});
            skLineSegment(sketch, "E388", {"start": v(6.49, -15.96) * mm, "end": v(8.55, -16.78) * mm});
            skLineSegment(sketch, "E389", {"start": v(23.45, 14.9) * mm, "end": v(21.5, 15.96) * mm});
            skLineSegment(sketch, "E390", {"start": v(25.24, -13.6) * mm, "end": v(26.86, -12.08) * mm});
            skLineSegment(sketch, "E391", {"start": v(28.27, -10.37) * mm, "end": v(29.46, -8.5) * mm});
            skLineSegment(sketch, "E392", {"start": v(-0.27, 10.37) * mm, "end": v(-1.46, 8.5) * mm});
            skLineSegment(sketch, "E393", {"start": v(1.14, 12.08) * mm, "end": v(-0.27, 10.37) * mm});
            skLineSegment(sketch, "E394", {"start": v(23.45, -14.9) * mm, "end": v(25.24, -13.6) * mm});
            skLineSegment(sketch, "E395", {"start": v(30.4, -6.5) * mm, "end": v(31.08, -4.39) * mm});
            skLineSegment(sketch, "E396", {"start": v(17.3, -17.33) * mm, "end": v(19.45, -16.78) * mm});
            skLineSegment(sketch, "E397", {"start": v(-2.4, 6.5) * mm, "end": v(-3.09, 4.39) * mm});
            skLineSegment(sketch, "E398", {"start": v(31.5, 2.21) * mm, "end": v(31.08, 4.39) * mm});
            skLineSegment(sketch, "E399", {"start": v(31.08, -4.39) * mm, "end": v(31.5, -2.21) * mm});
            skLineSegment(sketch, "E400", {"start": v(29.46, 8.5) * mm, "end": v(28.27, 10.37) * mm});
            skLineSegment(sketch, "E401", {"start": v(26.86, 12.08) * mm, "end": v(25.24, 13.6) * mm});
            skLineSegment(sketch, "E402", {"start": v(31.08, 4.39) * mm, "end": v(30.4, 6.5) * mm});
            skLineSegment(sketch, "E403", {"start": v(31.5, -2.21) * mm, "end": v(31.64, 0) * mm});
            skLineSegment(sketch, "E404", {"start": v(31.64, 0) * mm, "end": v(31.5, 2.21) * mm});
            skLineSegment(sketch, "E405", {"start": v(28.27, 10.37) * mm, "end": v(26.86, 12.08) * mm});
            skLineSegment(sketch, "E406", {"start": v(30.4, 6.5) * mm, "end": v(29.46, 8.5) * mm});
            skLineSegment(sketch, "E407", {"start": v(25.24, 13.6) * mm, "end": v(23.45, 14.9) * mm});
            skLineSegment(sketch, "E408", {"start": v(13.33, 18.55) * mm, "end": v(13.41, 18.48) * mm});
            skLineSegment(sketch, "E409", {"start": v(27.4, 13) * mm, "end": v(27.34, 12.9) * mm});
            skLineSegment(sketch, "E410", {"start": v(27.58, 13.2) * mm, "end": v(27.4, 13) * mm});
            skLineSegment(sketch, "E411", {"start": v(27.9, 16.18) * mm, "end": v(27.47, 16) * mm});
            skLineSegment(sketch, "E412", {"start": v(27.82, 13.54) * mm, "end": v(28.15, 14.16) * mm});
            skLineSegment(sketch, "E413", {"start": v(28.64, 15.52) * mm, "end": v(27.9, 16.18) * mm});
            skLineSegment(sketch, "E414", {"start": v(28.15, 14.16) * mm, "end": v(28.5, 15.07) * mm});
            skLineSegment(sketch, "E415", {"start": v(28.5, 15.07) * mm, "end": v(28.64, 15.52) * mm});
            skLineSegment(sketch, "E416", {"start": v(27.34, 12.9) * mm, "end": v(27.34, 12.8) * mm});
            skLineSegment(sketch, "E417", {"start": v(30.4, 8.7) * mm, "end": v(30.3, 8.73) * mm});
            skLineSegment(sketch, "E418", {"start": v(17.22, 19.08) * mm, "end": v(17.12, 19.77) * mm});
            skLineSegment(sketch, "E419", {"start": v(29.73, 9.85) * mm, "end": v(29.8, 9.93) * mm});
            skLineSegment(sketch, "E420", {"start": v(30.22, 8.8) * mm, "end": v(29.74, 9.64) * mm});
            skLineSegment(sketch, "E421", {"start": v(30.3, 8.73) * mm, "end": v(30.22, 8.8) * mm});
            skLineSegment(sketch, "E422", {"start": v(0.1, -16.18) * mm, "end": v(0.52, -16) * mm});
            skLineSegment(sketch, "E423", {"start": v(1.4, 15.55) * mm, "end": v(0.52, 16) * mm});
            skLineSegment(sketch, "E424", {"start": v(31.52, 6.43) * mm, "end": v(31.77, 6.53) * mm});
            skLineSegment(sketch, "E425", {"start": v(31.43, 6.37) * mm, "end": v(31.52, 6.43) * mm});
            skLineSegment(sketch, "E426", {"start": v(32.13, 6.75) * mm, "end": v(32.68, 7.18) * mm});
            skLineSegment(sketch, "E427", {"start": v(30.74, 8.84) * mm, "end": v(30.5, 8.72) * mm});
            skLineSegment(sketch, "E428", {"start": v(33.28, 9.12) * mm, "end": v(32.82, 9.14) * mm});
            skLineSegment(sketch, "E429", {"start": v(30.78, 10.9) * mm, "end": v(31.32, 11.73) * mm});
            skLineSegment(sketch, "E430", {"start": v(24.54, -15.73) * mm, "end": v(24.4, -15.5) * mm});
            skLineSegment(sketch, "E431", {"start": v(6.88, 18) * mm, "end": v(6.96, 17.58) * mm});
            skLineSegment(sketch, "E432", {"start": v(24.7, -16.12) * mm, "end": v(24.54, -15.73) * mm});
            skLineSegment(sketch, "E433", {"start": v(-3.53, -6.43) * mm, "end": v(-3.77, -6.53) * mm});
            skLineSegment(sketch, "E434", {"start": v(18.82, -18.74) * mm, "end": v(19.19, -19.33) * mm});
            skLineSegment(sketch, "E435", {"start": v(33.38, 7.87) * mm, "end": v(33.68, 8.23) * mm});
            skLineSegment(sketch, "E436", {"start": v(32.68, 7.18) * mm, "end": v(33.38, 7.87) * mm});
            skLineSegment(sketch, "E437", {"start": v(6.83, 18.69) * mm, "end": v(6.88, 18) * mm});
            skLineSegment(sketch, "E438", {"start": v(5.4, 17.33) * mm, "end": v(4.9, 17.83) * mm});
            skLineSegment(sketch, "E439", {"start": v(29.7, 9.75) * mm, "end": v(29.73, 9.85) * mm});
            skLineSegment(sketch, "E440", {"start": v(31.77, 6.53) * mm, "end": v(32.13, 6.75) * mm});
            skLineSegment(sketch, "E441", {"start": v(21.12, -19.67) * mm, "end": v(21.17, -18.69) * mm});
            skLineSegment(sketch, "E442", {"start": v(24.36, -15.4) * mm, "end": v(24.38, -15.3) * mm});
            skLineSegment(sketch, "E443", {"start": v(5.4, -17.33) * mm, "end": v(5.65, -17) * mm});
            skLineSegment(sketch, "E444", {"start": v(0.52, -16) * mm, "end": v(1.4, -15.55) * mm});
            skLineSegment(sketch, "E445", {"start": v(22.22, -16.76) * mm, "end": v(22.35, -17) * mm});
            skLineSegment(sketch, "E446", {"start": v(-5.77, -3.14) * mm, "end": v(-6.6, -3.67) * mm});
            skLineSegment(sketch, "E447", {"start": v(9.44, -18.1) * mm, "end": v(9.49, -18) * mm});
            skLineSegment(sketch, "E448", {"start": v(31.84, 9.08) * mm, "end": v(31.15, 8.96) * mm});
            skLineSegment(sketch, "E449", {"start": v(33.68, 8.23) * mm, "end": v(33.28, 9.12) * mm});
            skLineSegment(sketch, "E450", {"start": v(34.96, -3.95) * mm, "end": v(34.6, -3.67) * mm});
            skLineSegment(sketch, "E451", {"start": v(21.06, -20.13) * mm, "end": v(21.12, -19.67) * mm});
            skLineSegment(sketch, "E452", {"start": v(31.15, 8.96) * mm, "end": v(30.74, 8.84) * mm});
            skLineSegment(sketch, "E453", {"start": v(2.56, 14.62) * mm, "end": v(2.47, 14.68) * mm});
            skLineSegment(sketch, "E454", {"start": v(5.84, -16.67) * mm, "end": v(5.95, -16.64) * mm});
            skLineSegment(sketch, "E455", {"start": v(32.82, 9.14) * mm, "end": v(31.84, 9.08) * mm});
            skLineSegment(sketch, "E456", {"start": v(0.66, -12.9) * mm, "end": v(0.6, -13) * mm});
            skLineSegment(sketch, "E457", {"start": v(0.66, -12.8) * mm, "end": v(0.66, -12.9) * mm});
            skLineSegment(sketch, "E458", {"start": v(29.8, 9.93) * mm, "end": v(30.02, 10.08) * mm});
            skLineSegment(sketch, "E459", {"start": v(2.56, -14.62) * mm, "end": v(2.66, -14.6) * mm});
            skLineSegment(sketch, "E460", {"start": v(2.3, -14.88) * mm, "end": v(2.47, -14.68) * mm});
            skLineSegment(sketch, "E461", {"start": v(9.18, -18.74) * mm, "end": v(9.36, -18.36) * mm});
            skLineSegment(sketch, "E462", {"start": v(8.2, -20.1) * mm, "end": v(8.81, -19.33) * mm});
            skLineSegment(sketch, "E463", {"start": v(8.81, -19.33) * mm, "end": v(9.18, -18.74) * mm});
            skLineSegment(sketch, "E464", {"start": v(1.4, -15.55) * mm, "end": v(1.98, -15.16) * mm});
            skLineSegment(sketch, "E465", {"start": v(2.47, -14.68) * mm, "end": v(2.56, -14.62) * mm});
            skLineSegment(sketch, "E466", {"start": v(7.88, -20.44) * mm, "end": v(8.2, -20.1) * mm});
            skLineSegment(sketch, "E467", {"start": v(1.98, -15.16) * mm, "end": v(2.3, -14.88) * mm});
            skLineSegment(sketch, "E468", {"start": v(0.42, -13.2) * mm, "end": v(0.18, -13.54) * mm});
            skLineSegment(sketch, "E469", {"start": v(0.6, -13) * mm, "end": v(0.42, -13.2) * mm});
            skLineSegment(sketch, "E470", {"start": v(2.76, -14.64) * mm, "end": v(3.54, -15.21) * mm});
            skLineSegment(sketch, "E471", {"start": v(-1.56, 12.6) * mm, "end": v(-2.5, 12.85) * mm});
            skLineSegment(sketch, "E472", {"start": v(-6.96, -3.95) * mm, "end": v(-6.76, -4.92) * mm});
            skLineSegment(sketch, "E473", {"start": v(-0.91, 12.33) * mm, "end": v(-1.56, 12.6) * mm});
            skLineSegment(sketch, "E474", {"start": v(-0.54, 12.12) * mm, "end": v(-0.91, 12.33) * mm});
            skLineSegment(sketch, "E475", {"start": v(29.56, -12.6) * mm, "end": v(30.5, -12.85) * mm});
            skLineSegment(sketch, "E476", {"start": v(30.02, 10.08) * mm, "end": v(30.33, 10.37) * mm});
            skLineSegment(sketch, "E477", {"start": v(-6.6, -3.67) * mm, "end": v(-6.96, -3.95) * mm});
            skLineSegment(sketch, "E478", {"start": v(31.77, -6.53) * mm, "end": v(31.52, -6.43) * mm});
            skLineSegment(sketch, "E479", {"start": v(-0.33, 11.96) * mm, "end": v(-0.54, 12.12) * mm});
            skLineSegment(sketch, "E480", {"start": v(30.33, 10.37) * mm, "end": v(30.78, 10.9) * mm});
            skLineSegment(sketch, "E481", {"start": v(30.96, 12.93) * mm, "end": v(30.5, 12.85) * mm});
            skLineSegment(sketch, "E482", {"start": v(28.15, -14.16) * mm, "end": v(27.82, -13.54) * mm});
            skLineSegment(sketch, "E483", {"start": v(-0.15, -14.16) * mm, "end": v(-0.5, -15.07) * mm});
            skLineSegment(sketch, "E484", {"start": v(14.7, -18.65) * mm, "end": v(14.72, -18.92) * mm});
            skLineSegment(sketch, "E485", {"start": v(0.18, -13.54) * mm, "end": v(-0.15, -14.16) * mm});
            skLineSegment(sketch, "E486", {"start": v(3.61, -15.3) * mm, "end": v(3.64, -15.4) * mm});
            skLineSegment(sketch, "E487", {"start": v(27.82, -13.54) * mm, "end": v(27.58, -13.2) * mm});
            skLineSegment(sketch, "E488", {"start": v(12.95, -19.99) * mm, "end": v(13.18, -19.33) * mm});
            skLineSegment(sketch, "E489", {"start": v(31.54, 12.14) * mm, "end": v(30.96, 12.93) * mm});
            skLineSegment(sketch, "E490", {"start": v(14.72, -18.92) * mm, "end": v(14.81, -19.33) * mm});
            skLineSegment(sketch, "E491", {"start": v(28.5, -15.07) * mm, "end": v(28.15, -14.16) * mm});
            skLineSegment(sketch, "E492", {"start": v(30.78, -10.9) * mm, "end": v(30.33, -10.37) * mm});
            skLineSegment(sketch, "E493", {"start": v(31.32, 11.73) * mm, "end": v(31.54, 12.14) * mm});
            skLineSegment(sketch, "E494", {"start": v(31.4, -6.16) * mm, "end": v(31.7, -5.24) * mm});
            skLineSegment(sketch, "E495", {"start": v(17.12, -19.77) * mm, "end": v(17.22, -19.08) * mm});
            skLineSegment(sketch, "E496", {"start": v(29.56, 12.6) * mm, "end": v(28.9, 12.33) * mm});
            skLineSegment(sketch, "E497", {"start": v(28.12, 11.93) * mm, "end": v(28.03, 11.99) * mm});
            skLineSegment(sketch, "E498", {"start": v(14.67, -18.55) * mm, "end": v(14.7, -18.65) * mm});
            skLineSegment(sketch, "E499", {"start": v(13.52, -18.45) * mm, "end": v(14.48, -18.45) * mm});
            skLineSegment(sketch, "E500", {"start": v(28.54, 12.12) * mm, "end": v(28.33, 11.96) * mm});
            skLineSegment(sketch, "E501", {"start": v(28.33, 11.96) * mm, "end": v(28.23, 11.92) * mm});
            skLineSegment(sketch, "E502", {"start": v(16.87, -20.72) * mm, "end": v(17.12, -19.77) * mm});
            skLineSegment(sketch, "E503", {"start": v(28.9, 12.33) * mm, "end": v(28.54, 12.12) * mm});
            skLineSegment(sketch, "E504", {"start": v(17.22, -19.08) * mm, "end": v(17.23, -18.66) * mm});
            skLineSegment(sketch, "E505", {"start": v(28.23, 11.92) * mm, "end": v(28.12, 11.93) * mm});
            skLineSegment(sketch, "E506", {"start": v(16.72, -21.16) * mm, "end": v(16.87, -20.72) * mm});
            skLineSegment(sketch, "E507", {"start": v(30.5, 12.85) * mm, "end": v(29.56, 12.6) * mm});
            skLineSegment(sketch, "E508", {"start": v(29.56, -12.6) * mm, "end": v(28.9, -12.33) * mm});
            skLineSegment(sketch, "E509", {"start": v(31.43, -6.37) * mm, "end": v(31.52, -6.43) * mm});
            skLineSegment(sketch, "E510", {"start": v(31.15, -8.96) * mm, "end": v(30.74, -8.84) * mm});
            skLineSegment(sketch, "E511", {"start": v(30.74, -8.84) * mm, "end": v(30.5, -8.72) * mm});
            skLineSegment(sketch, "E512", {"start": v(32.44, -1.35) * mm, "end": v(32.4, -1.43) * mm});
            skLineSegment(sketch, "E513", {"start": v(34.76, -4.92) * mm, "end": v(34.3, -5.02) * mm});
            skLineSegment(sketch, "E514", {"start": v(35.33, -0.5) * mm, "end": v(34.9, -0.7) * mm});
            skLineSegment(sketch, "E515", {"start": v(33.14, -2.83) * mm, "end": v(33.77, -3.14) * mm});
            skLineSegment(sketch, "E516", {"start": v(32.74, -2.7) * mm, "end": v(33.14, -2.83) * mm});
            skLineSegment(sketch, "E517", {"start": v(33.77, -3.14) * mm, "end": v(34.6, -3.67) * mm});
            skLineSegment(sketch, "E518", {"start": v(32.62, -1.25) * mm, "end": v(32.52, -1.28) * mm});
            skLineSegment(sketch, "E519", {"start": v(33.99, -1.04) * mm, "end": v(33.3, -1.2) * mm});
            skLineSegment(sketch, "E520", {"start": v(35.33, 0.5) * mm, "end": v(35.33, -0.5) * mm});
            skLineSegment(sketch, "E521", {"start": v(34.9, 0.7) * mm, "end": v(35.33, 0.5) * mm});
            skLineSegment(sketch, "E522", {"start": v(32.38, -2.6) * mm, "end": v(32.48, -2.65) * mm});
            skLineSegment(sketch, "E523", {"start": v(32.62, 1.25) * mm, "end": v(32.9, 1.26) * mm});
            skLineSegment(sketch, "E524", {"start": v(33.3, -1.2) * mm, "end": v(32.9, -1.26) * mm});
            skLineSegment(sketch, "E525", {"start": v(32.31, -2.53) * mm, "end": v(32.38, -2.6) * mm});
            skLineSegment(sketch, "E526", {"start": v(32.52, 1.28) * mm, "end": v(32.62, 1.25) * mm});
            skLineSegment(sketch, "E527", {"start": v(32.9, -1.26) * mm, "end": v(32.62, -1.25) * mm});
            skLineSegment(sketch, "E528", {"start": v(32.48, -2.65) * mm, "end": v(32.74, -2.7) * mm});
            skLineSegment(sketch, "E529", {"start": v(32.44, 1.35) * mm, "end": v(32.52, 1.28) * mm});
            skLineSegment(sketch, "E530", {"start": v(32.4, 1.43) * mm, "end": v(32.44, 1.35) * mm});
            skLineSegment(sketch, "E531", {"start": v(32.9, 1.26) * mm, "end": v(33.3, 1.2) * mm});
            skLineSegment(sketch, "E532", {"start": v(33.3, 1.2) * mm, "end": v(33.99, 1.04) * mm});
            skLineSegment(sketch, "E533", {"start": v(33.99, 1.04) * mm, "end": v(34.9, 0.7) * mm});
            skLineSegment(sketch, "E534", {"start": v(32.52, -1.28) * mm, "end": v(32.44, -1.35) * mm});
            skLineSegment(sketch, "E535", {"start": v(34.9, -0.7) * mm, "end": v(33.99, -1.04) * mm});
            skLineSegment(sketch, "E536", {"start": v(31.4, 6.16) * mm, "end": v(31.7, 5.24) * mm});
            skLineSegment(sketch, "E537", {"start": v(31.75, 5.15) * mm, "end": v(31.85, 5.1) * mm});
            skLineSegment(sketch, "E538", {"start": v(32.22, -5.16) * mm, "end": v(31.96, -5.1) * mm});
            skLineSegment(sketch, "E539", {"start": v(33.14, 2.83) * mm, "end": v(32.74, 2.7) * mm});
            skLineSegment(sketch, "E540", {"start": v(32.38, 2.6) * mm, "end": v(32.31, 2.52) * mm});
            skLineSegment(sketch, "E541", {"start": v(32.74, 2.7) * mm, "end": v(32.48, 2.65) * mm});
            skLineSegment(sketch, "E542", {"start": v(32.48, 2.65) * mm, "end": v(32.38, 2.6) * mm});
            skLineSegment(sketch, "E543", {"start": v(34.3, 5.02) * mm, "end": v(34.76, 4.92) * mm});
            skLineSegment(sketch, "E544", {"start": v(31.43, 6.37) * mm, "end": v(31.39, 6.27) * mm});
            skLineSegment(sketch, "E545", {"start": v(34.76, 4.92) * mm, "end": v(34.96, 3.95) * mm});
            skLineSegment(sketch, "E546", {"start": v(31.96, 5.1) * mm, "end": v(32.22, 5.16) * mm});
            skLineSegment(sketch, "E547", {"start": v(33.77, 3.14) * mm, "end": v(33.14, 2.83) * mm});
            skLineSegment(sketch, "E548", {"start": v(32.22, 5.16) * mm, "end": v(32.63, 5.2) * mm});
            skLineSegment(sketch, "E549", {"start": v(33.33, 5.17) * mm, "end": v(34.3, 5.02) * mm});
            skLineSegment(sketch, "E550", {"start": v(32.3, 2.4) * mm, "end": v(32.31, 2.52) * mm});
            skLineSegment(sketch, "E551", {"start": v(32.3, -2.4) * mm, "end": v(32.31, -2.53) * mm});
            skLineSegment(sketch, "E552", {"start": v(32.63, 5.2) * mm, "end": v(33.33, 5.17) * mm});
            skLineSegment(sketch, "E553", {"start": v(5.77, 16.76) * mm, "end": v(5.65, 17) * mm});
            skLineSegment(sketch, "E554", {"start": v(-0.64, 15.52) * mm, "end": v(0.1, 16.18) * mm});
            skLineSegment(sketch, "E555", {"start": v(-3.4, -6.27) * mm, "end": v(-3.44, -6.37) * mm});
            skLineSegment(sketch, "E556", {"start": v(25.09, -18.22) * mm, "end": v(24.24, -18.72) * mm});
            skLineSegment(sketch, "E557", {"start": v(10.78, -19.08) * mm, "end": v(10.77, -18.66) * mm});
            skLineSegment(sketch, "E558", {"start": v(-1.56, -12.6) * mm, "end": v(-2.5, -12.85) * mm});
            skLineSegment(sketch, "E559", {"start": v(18.64, -18.36) * mm, "end": v(18.82, -18.74) * mm});
            skLineSegment(sketch, "E560", {"start": v(27.34, -12.8) * mm, "end": v(27.34, -12.9) * mm});
            skLineSegment(sketch, "E561", {"start": v(-3.53, -6.43) * mm, "end": v(-3.44, -6.37) * mm});
            skLineSegment(sketch, "E562", {"start": v(-2.5, -12.85) * mm, "end": v(-2.97, -12.93) * mm});
            skLineSegment(sketch, "E563", {"start": v(-0.64, -15.52) * mm, "end": v(-0.5, -15.07) * mm});
            skLineSegment(sketch, "E564", {"start": v(-0.91, -12.33) * mm, "end": v(-1.56, -12.6) * mm});
            skLineSegment(sketch, "E565", {"start": v(21.06, -20.13) * mm, "end": v(20.12, -20.44) * mm});
            skLineSegment(sketch, "E566", {"start": v(30.02, -10.08) * mm, "end": v(30.33, -10.37) * mm});
            skLineSegment(sketch, "E567", {"start": v(0.1, -16.18) * mm, "end": v(-0.64, -15.52) * mm});
            skLineSegment(sketch, "E568", {"start": v(14.81, -19.33) * mm, "end": v(15.05, -19.99) * mm});
            skLineSegment(sketch, "E569", {"start": v(-0.54, -12.12) * mm, "end": v(-0.91, -12.33) * mm});
            skLineSegment(sketch, "E570", {"start": v(-0.33, -11.96) * mm, "end": v(-0.54, -12.12) * mm});
            skLineSegment(sketch, "E571", {"start": v(-1.73, -9.85) * mm, "end": v(-1.8, -9.93) * mm});
            skLineSegment(sketch, "E572", {"start": v(31.54, -12.14) * mm, "end": v(30.96, -12.93) * mm});
            skLineSegment(sketch, "E573", {"start": v(-1.7, -9.75) * mm, "end": v(-1.73, -9.85) * mm});
            skLineSegment(sketch, "E574", {"start": v(-1.74, -9.64) * mm, "end": v(-1.7, -9.75) * mm});
            skLineSegment(sketch, "E575", {"start": v(9.58, -17.95) * mm, "end": v(9.49, -18) * mm});
            skLineSegment(sketch, "E576", {"start": v(19.8, -20.1) * mm, "end": v(19.19, -19.33) * mm});
            skLineSegment(sketch, "E577", {"start": v(29.8, -9.93) * mm, "end": v(30.02, -10.08) * mm});
            skLineSegment(sketch, "E578", {"start": v(29.73, -9.85) * mm, "end": v(29.8, -9.93) * mm});
            skLineSegment(sketch, "E579", {"start": v(30.96, -12.93) * mm, "end": v(30.5, -12.85) * mm});
            skLineSegment(sketch, "E580", {"start": v(-0.23, -11.92) * mm, "end": v(-0.33, -11.96) * mm});
            skLineSegment(sketch, "E581", {"start": v(29.7, -9.75) * mm, "end": v(29.73, -9.85) * mm});
            skLineSegment(sketch, "E582", {"start": v(-5.3, 1.2) * mm, "end": v(-4.9, 1.26) * mm});
            skLineSegment(sketch, "E583", {"start": v(25.7, -14.88) * mm, "end": v(25.53, -14.68) * mm});
            skLineSegment(sketch, "E584", {"start": v(25.53, -14.68) * mm, "end": v(25.44, -14.62) * mm});
            skLineSegment(sketch, "E585", {"start": v(-4.13, -6.75) * mm, "end": v(-3.77, -6.53) * mm});
            skLineSegment(sketch, "E586", {"start": v(-0.12, -11.93) * mm, "end": v(-0.23, -11.92) * mm});
            skLineSegment(sketch, "E587", {"start": v(24.9, -16.8) * mm, "end": v(25.05, -17.76) * mm});
            skLineSegment(sketch, "E588", {"start": v(25.44, -14.62) * mm, "end": v(25.33, -14.6) * mm});
            skLineSegment(sketch, "E589", {"start": v(-4.44, -1.35) * mm, "end": v(-4.4, -1.45) * mm});
            skLineSegment(sketch, "E590", {"start": v(-4.69, -7.18) * mm, "end": v(-4.13, -6.75) * mm});
            skLineSegment(sketch, "E591", {"start": v(-3.32, -11.73) * mm, "end": v(-2.78, -10.9) * mm});
            skLineSegment(sketch, "E592", {"start": v(25.23, -14.64) * mm, "end": v(24.46, -15.21) * mm});
            skLineSegment(sketch, "E593", {"start": v(-0.12, 11.93) * mm, "end": v(0.51, 12.66) * mm});
            skLineSegment(sketch, "E594", {"start": v(-1.7, -9.75) * mm, "end": v(-2.21, -8.9) * mm});
            skLineSegment(sketch, "E595", {"start": v(-4.44, 1.35) * mm, "end": v(-4.35, 2.32) * mm});
            skLineSegment(sketch, "E596", {"start": v(28.12, 11.93) * mm, "end": v(27.48, 12.66) * mm});
            skLineSegment(sketch, "E597", {"start": v(9.64, 17.95) * mm, "end": v(9.7, 17.95) * mm});
            skLineSegment(sketch, "E598", {"start": v(9.7, 17.95) * mm, "end": v(10.18, 18.1) * mm});
            skLineSegment(sketch, "E599", {"start": v(32.4, 1.43) * mm, "end": v(32.35, 1.9) * mm});
            skLineSegment(sketch, "E600", {"start": v(32.35, 1.9) * mm, "end": v(32.37, 1.98) * mm});
            skLineSegment(sketch, "E601", {"start": v(9.64, -17.95) * mm, "end": v(9.7, -17.95) * mm});
            skLineSegment(sketch, "E602", {"start": v(9.7, -17.95) * mm, "end": v(10.18, -18.1) * mm});
            skLineSegment(sketch, "E603", {"start": v(32.37, -1.98) * mm, "end": v(32.35, -1.9) * mm});
            skLineSegment(sketch, "E604", {"start": v(32.35, -1.9) * mm, "end": v(32.4, -1.43) * mm});
            skLineSegment(sketch, "E605", {"start": v(-0.04, -11.99) * mm, "end": v(0.56, -12.65) * mm});
            skLineSegment(sketch, "E606", {"start": v(0.56, -12.65) * mm, "end": v(0.6, -12.7) * mm});
            skLineSegment(sketch, "E607", {"start": v(10.63, -18.15) * mm, "end": v(10.58, -18.14) * mm});
            skLineSegment(sketch, "E608", {"start": v(10.58, -18.14) * mm, "end": v(9.7, -17.95) * mm});
            skLineSegment(sketch, "E609", {"start": v(21.02, -17.09) * mm, "end": v(20.98, -17.12) * mm});
            skLineSegment(sketch, "E610", {"start": v(17.47, 18.17) * mm, "end": v(17.37, 18.18) * mm});
            skLineSegment(sketch, "E611", {"start": v(32.35, -2.27) * mm, "end": v(32.35, -2.32) * mm});
            skLineSegment(sketch, "E612", {"start": v(9.64, -17.95) * mm, "end": v(9.58, -17.95) * mm});
            skLineSegment(sketch, "E613", {"start": v(32.33, 2.41) * mm, "end": v(32.35, 2.32) * mm});
            skLineSegment(sketch, "E614", {"start": v(32.34, -2.06) * mm, "end": v(32.35, -1.9) * mm});
            skLineSegment(sketch, "E615", {"start": v(9.7, 17.95) * mm, "end": v(10.58, 18.14) * mm});
            skLineSegment(sketch, "E616", {"start": v(10.58, 18.14) * mm, "end": v(10.63, 18.15) * mm});
            skLineSegment(sketch, "E617", {"start": v(27.39, 12.7) * mm, "end": v(27.51, 12.57) * mm});
            skLineSegment(sketch, "E618", {"start": v(27.51, 12.57) * mm, "end": v(28.03, 11.99) * mm});
            skLineSegment(sketch, "E619", {"start": v(21.02, 17.09) * mm, "end": v(20.98, 17.12) * mm});
            skLineSegment(sketch, "E620", {"start": v(9.64, 17.95) * mm, "end": v(9.58, 17.95) * mm});
            skLineSegment(sketch, "E621", {"start": v(-4.4, -1.45) * mm, "end": v(-4.36, -1.9) * mm});
            skLineSegment(sketch, "E622", {"start": v(-4.36, -1.9) * mm, "end": v(-4.3, -2.4) * mm});
            skLineSegment(sketch, "E623", {"start": v(0.6, 12.7) * mm, "end": v(0.56, 12.65) * mm});
            skLineSegment(sketch, "E624", {"start": v(0.56, 12.65) * mm, "end": v(-0.04, 11.99) * mm});
            skLineSegment(sketch, "E625", {"start": v(-1.74, 9.64) * mm, "end": v(-2.17, 8.9) * mm});
            skLineSegment(sketch, "E626", {"start": v(-2.17, 8.9) * mm, "end": v(-2.22, 8.8) * mm});
            skLineSegment(sketch, "E627", {"start": v(6.95, 17.06) * mm, "end": v(6.17, 16.71) * mm});
            skLineSegment(sketch, "E628", {"start": v(6.17, 16.71) * mm, "end": v(6.05, 16.66) * mm});
            skLineSegment(sketch, "E629", {"start": v(-2.22, -8.8) * mm, "end": v(-2.17, -8.9) * mm});
            skLineSegment(sketch, "E630", {"start": v(-2.17, -8.9) * mm, "end": v(-1.74, -9.64) * mm});
            skLineSegment(sketch, "E631", {"start": v(4.55, -14.9) * mm, "end": v(4.59, -14.92) * mm});
            skLineSegment(sketch, "E632", {"start": v(4.59, -14.92) * mm, "end": v(6.49, -15.96) * mm});
            skLineSegment(sketch, "E633", {"start": v(-1.46, -8.5) * mm, "end": v(-1.43, -8.54) * mm});
            skLineSegment(sketch, "E634", {"start": v(-1.43, -8.54) * mm, "end": v(-0.27, -10.37) * mm});
            skLineSegment(sketch, "E635", {"start": v(32.34, -2.06) * mm, "end": v(32.3, -2.4) * mm});
            skLineSegment(sketch, "E636", {"start": v(32.3, 2.4) * mm, "end": v(32.37, 1.98) * mm});
            skLineSegment(sketch, "E637", {"start": v(32.35, 2.32) * mm, "end": v(32.35, 2.27) * mm});
            skLineSegment(sketch, "E638", {"start": v(17.79, 18.09) * mm, "end": v(17.5, 18.12) * mm});
            skLineSegment(sketch, "E639", {"start": v(17.5, 18.12) * mm, "end": v(17.36, 18.15) * mm});
            skLineSegment(sketch, "E640", {"start": v(6.05, -16.66) * mm, "end": v(6.17, -16.71) * mm});
            skLineSegment(sketch, "E641", {"start": v(6.17, -16.71) * mm, "end": v(6.43, -16.86) * mm});
            skLineSegment(sketch, "E642", {"start": v(-4.3, 2.4) * mm, "end": v(-4.34, 2.06) * mm});
            skLineSegment(sketch, "E643", {"start": v(17.36, -18.15) * mm, "end": v(17.5, -18.12) * mm});
            skLineSegment(sketch, "E644", {"start": v(17.5, -18.12) * mm, "end": v(17.79, -18.09) * mm});
            skLineSegment(sketch, "E645", {"start": v(27.39, -12.7) * mm, "end": v(27.51, -12.57) * mm});
            skLineSegment(sketch, "E646", {"start": v(27.51, -12.57) * mm, "end": v(27.7, -12.4) * mm});
            skLineSegment(sketch, "E647", {"start": v(21.05, -17.07) * mm, "end": v(21.86, -16.75) * mm});
            skLineSegment(sketch, "E648", {"start": v(-2.3, 8.73) * mm, "end": v(-2.21, 8.9) * mm});
            skLineSegment(sketch, "E649", {"start": v(5.95, -16.64) * mm, "end": v(6.13, -16.74) * mm});
            skLineSegment(sketch, "E650", {"start": v(21.05, 17.07) * mm, "end": v(21.86, 16.75) * mm});
            skLineSegment(sketch, "E651", {"start": v(-2.21, -8.9) * mm, "end": v(-2.3, -8.73) * mm});
            skLineSegment(sketch, "E652", {"start": v(30.3, 8.73) * mm, "end": v(30.21, 8.9) * mm});
            skLineSegment(sketch, "E653", {"start": v(31.4, 6.16) * mm, "end": v(31.39, 6.27) * mm});
            skLineSegment(sketch, "E654", {"start": v(31.7, 5.24) * mm, "end": v(31.75, 5.15) * mm});
            skLineSegment(sketch, "E655", {"start": v(3.54, -15.21) * mm, "end": v(3.61, -15.3) * mm});
            skLineSegment(sketch, "E656", {"start": v(2.76, -14.64) * mm, "end": v(2.66, -14.6) * mm});
            skLineSegment(sketch, "E657", {"start": v(-3.75, -5.15) * mm, "end": v(-3.7, -5.24) * mm});
            skLineSegment(sketch, "E658", {"start": v(-3.4, -6.16) * mm, "end": v(-3.4, -6.27) * mm});
            skLineSegment(sketch, "E659", {"start": v(31.4, -6.16) * mm, "end": v(31.39, -6.27) * mm});
            skLineSegment(sketch, "E660", {"start": v(31.7, -5.24) * mm, "end": v(31.75, -5.15) * mm});
            skLineSegment(sketch, "E661", {"start": v(24.46, -15.21) * mm, "end": v(24.38, -15.3) * mm});
            skLineSegment(sketch, "E662", {"start": v(25.33, -14.6) * mm, "end": v(25.23, -14.64) * mm});
            skLineSegment(sketch, "E663", {"start": v(-3.4, 6.27) * mm, "end": v(-3.4, 6.16) * mm});
            skLineSegment(sketch, "E664", {"start": v(-3.7, 5.24) * mm, "end": v(-3.75, 5.15) * mm});
            skLineSegment(sketch, "E665", {"start": v(13.52, -18.45) * mm, "end": v(13.41, -18.48) * mm});
            skLineSegment(sketch, "E666", {"start": v(14.48, -18.45) * mm, "end": v(14.59, -18.48) * mm});
            skLineSegment(sketch, "E667", {"start": v(25.33, 14.6) * mm, "end": v(25.23, 14.64) * mm});
            skLineSegment(sketch, "E668", {"start": v(24.46, 15.21) * mm, "end": v(24.38, 15.3) * mm});
            skLineSegment(sketch, "E669", {"start": v(2.76, 14.64) * mm, "end": v(2.66, 14.6) * mm});
            skLineSegment(sketch, "E670", {"start": v(3.54, 15.21) * mm, "end": v(3.61, 15.3) * mm});
            skLineSegment(sketch, "E671", {"start": v(-4.34, 2.06) * mm, "end": v(-4.4, 1.45) * mm});
            skLineSegment(sketch, "E672", {"start": v(29.74, 9.64) * mm, "end": v(29.7, 9.75) * mm});
            skLineSegment(sketch, "E673", {"start": v(13.41, 18.48) * mm, "end": v(13.52, 18.45) * mm});
            skLineSegment(sketch, "E674", {"start": v(14.48, 18.45) * mm, "end": v(14.59, 18.48) * mm});
            skLineSegment(sketch, "E675", {"start": v(14, 1.75) * mm, "end": v(14, -1.75) * mm});
            skPoint(sketch, "E676", {"position": v(14, 0) * mm});
            skSolve(sketch);
        }
        {
            var Q0;
            Q0=makeQuery(id+"F0.imprint","IMPRINT",FACE,{"disambiguationData":[TD([[makeQuery(id+"F0.imprint","IMPRINT",EDGE,{"derivedFrom":sQuery(id+"F0.wireOp",EDGE,"E2")}),1.0]])]});
            var Q1;
            Q1=makeQuery(id+"F0.imprint","IMPRINT",FACE,{"disambiguationData":[TD([[makeQuery(id+"F0.imprint","IMPRINT",EDGE,{"derivedFrom":sQuery(id+"F0.wireOp",EDGE,"E110")}),1.0]])]});
            extrude(context, id + "F1", {"entities" : qUnion([Q0, Q1]), "depth" : 5.4 * mm, "offsetDistance" : 25 * mm});
        }
        {
            var Q0;
            Q0=makeQuery(id+"F1.opExtrude","CAP_FACE",FACE,{"disambiguationData":[OSD([sQuery(id+"F0.wireOp",EDGE,"E2"),sQuery(id+"F0.wireOp",EDGE,"E8"),sQuery(id+"F0.wireOp",EDGE,"E10"),sQuery(id+"F0.wireOp",EDGE,"E21"),sQuery(id+"F0.wireOp",EDGE,"E22"),sQuery(id+"F0.wireOp",EDGE,"E27"),sQuery(id+"F0.wireOp",EDGE,"E28"),sQuery(id+"F0.wireOp",EDGE,"E29"),sQuery(id+"F0.wireOp",EDGE,"E30"),sQuery(id+"F0.wireOp",EDGE,"E31"),sQuery(id+"F0.wireOp",EDGE,"E32"),sQuery(id+"F0.wireOp",EDGE,"E33"),sQuery(id+"F0.wireOp",EDGE,"E34"),sQuery(id+"F0.wireOp",EDGE,"E35"),sQuery(id+"F0.wireOp",EDGE,"E36"),sQuery(id+"F0.wireOp",EDGE,"E37"),sQuery(id+"F0.wireOp",EDGE,"E38"),sQuery(id+"F0.wireOp",EDGE,"E39"),sQuery(id+"F0.wireOp",EDGE,"E40"),sQuery(id+"F0.wireOp",EDGE,"E41"),sQuery(id+"F0.wireOp",EDGE,"E42"),sQuery(id+"F0.wireOp",EDGE,"E43"),sQuery(id+"F0.wireOp",EDGE,"E44"),sQuery(id+"F0.wireOp",EDGE,"E45"),sQuery(id+"F0.wireOp",EDGE,"E46"),sQuery(id+"F0.wireOp",EDGE,"E47"),sQuery(id+"F0.wireOp",EDGE,"E48"),sQuery(id+"F0.wireOp",EDGE,"E49"),sQuery(id+"F0.wireOp",EDGE,"E50"),sQuery(id+"F0.wireOp",EDGE,"E51"),sQuery(id+"F0.wireOp",EDGE,"E52"),sQuery(id+"F0.wireOp",EDGE,"E53"),sQuery(id+"F0.wireOp",EDGE,"E54"),sQuery(id+"F0.wireOp",EDGE,"E55"),sQuery(id+"F0.wireOp",EDGE,"E56"),sQuery(id+"F0.wireOp",EDGE,"E57"),sQuery(id+"F0.wireOp",EDGE,"E58"),sQuery(id+"F0.wireOp",EDGE,"E59"),sQuery(id+"F0.wireOp",EDGE,"E60"),sQuery(id+"F0.wireOp",EDGE,"E61"),sQuery(id+"F0.wireOp",EDGE,"E62"),sQuery(id+"F0.wireOp",EDGE,"E63"),sQuery(id+"F0.wireOp",EDGE,"E64"),sQuery(id+"F0.wireOp",EDGE,"E65"),sQuery(id+"F0.wireOp",EDGE,"E66"),sQuery(id+"F0.wireOp",EDGE,"E83"),sQuery(id+"F0.wireOp",EDGE,"E84"),sQuery(id+"F0.wireOp",EDGE,"E85"),sQuery(id+"F0.wireOp",EDGE,"E86"),sQuery(id+"F0.wireOp",EDGE,"E87"),sQuery(id+"F0.wireOp",EDGE,"E88"),sQuery(id+"F0.wireOp",EDGE,"E89"),sQuery(id+"F0.wireOp",EDGE,"E90"),sQuery(id+"F0.wireOp",EDGE,"E91"),sQuery(id+"F0.wireOp",EDGE,"E92"),sQuery(id+"F0.wireOp",EDGE,"E93"),sQuery(id+"F0.wireOp",EDGE,"E94"),sQuery(id+"F0.wireOp",EDGE,"E95"),sQuery(id+"F0.wireOp",EDGE,"E96"),sQuery(id+"F0.wireOp",EDGE,"E97"),sQuery(id+"F0.wireOp",EDGE,"E98"),sQuery(id+"F0.wireOp",EDGE,"E99"),sQuery(id+"F0.wireOp",EDGE,"E100"),sQuery(id+"F0.wireOp",EDGE,"E101"),sQuery(id+"F0.wireOp",EDGE,"E102"),sQuery(id+"F0.wireOp",EDGE,"E103"),sQuery(id+"F0.wireOp",EDGE,"E104"),sQuery(id+"F0.wireOp",EDGE,"E105"),sQuery(id+"F0.wireOp",EDGE,"E106"),sQuery(id+"F0.wireOp",EDGE,"E107"),sQuery(id+"F0.wireOp",EDGE,"E108"),sQuery(id+"F0.wireOp",EDGE,"E109"),sQuery(id+"F0.wireOp",EDGE,"E116"),sQuery(id+"F0.wireOp",EDGE,"E117"),sQuery(id+"F0.wireOp",EDGE,"E119"),sQuery(id+"F0.wireOp",EDGE,"E120"),sQuery(id+"F0.wireOp",EDGE,"E122"),sQuery(id+"F0.wireOp",EDGE,"E123"),sQuery(id+"F0.wireOp",EDGE,"E124"),sQuery(id+"F0.wireOp",EDGE,"E125"),sQuery(id+"F0.wireOp",EDGE,"E126"),sQuery(id+"F0.wireOp",EDGE,"E127"),sQuery(id+"F0.wireOp",EDGE,"E128"),sQuery(id+"F0.wireOp",EDGE,"E129"),sQuery(id+"F0.wireOp",EDGE,"E130"),sQuery(id+"F0.wireOp",EDGE,"E131"),sQuery(id+"F0.wireOp",EDGE,"E132"),sQuery(id+"F0.wireOp",EDGE,"E133"),sQuery(id+"F0.wireOp",EDGE,"E134"),sQuery(id+"F0.wireOp",EDGE,"E135"),sQuery(id+"F0.wireOp",EDGE,"E136"),sQuery(id+"F0.wireOp",EDGE,"E137"),sQuery(id+"F0.wireOp",EDGE,"E138"),sQuery(id+"F0.wireOp",EDGE,"E139"),sQuery(id+"F0.wireOp",EDGE,"E140"),sQuery(id+"F0.wireOp",EDGE,"E141"),sQuery(id+"F0.wireOp",EDGE,"E142"),sQuery(id+"F0.wireOp",EDGE,"E143"),sQuery(id+"F0.wireOp",EDGE,"E144"),sQuery(id+"F0.wireOp",EDGE,"E145"),sQuery(id+"F0.wireOp",EDGE,"E146"),sQuery(id+"F0.wireOp",EDGE,"E147"),sQuery(id+"F0.wireOp",EDGE,"E148"),sQuery(id+"F0.wireOp",EDGE,"E149"),sQuery(id+"F0.wireOp",EDGE,"E150"),sQuery(id+"F0.wireOp",EDGE,"E151"),sQuery(id+"F0.wireOp",EDGE,"E152"),sQuery(id+"F0.wireOp",EDGE,"E153"),sQuery(id+"F0.wireOp",EDGE,"E154"),sQuery(id+"F0.wireOp",EDGE,"E155"),sQuery(id+"F0.wireOp",EDGE,"E156"),sQuery(id+"F0.wireOp",EDGE,"E157"),sQuery(id+"F0.wireOp",EDGE,"E158"),sQuery(id+"F0.wireOp",EDGE,"E159"),sQuery(id+"F0.wireOp",EDGE,"E160"),sQuery(id+"F0.wireOp",EDGE,"E161"),sQuery(id+"F0.wireOp",EDGE,"E162"),sQuery(id+"F0.wireOp",EDGE,"E163"),sQuery(id+"F0.wireOp",EDGE,"E164"),sQuery(id+"F0.wireOp",EDGE,"E165"),sQuery(id+"F0.wireOp",EDGE,"E166"),sQuery(id+"F0.wireOp",EDGE,"E167"),sQuery(id+"F0.wireOp",EDGE,"E168"),sQuery(id+"F0.wireOp",EDGE,"E169"),sQuery(id+"F0.wireOp",EDGE,"E170"),sQuery(id+"F0.wireOp",EDGE,"E171"),sQuery(id+"F0.wireOp",EDGE,"E172"),sQuery(id+"F0.wireOp",EDGE,"E173"),sQuery(id+"F0.wireOp",EDGE,"E174"),sQuery(id+"F0.wireOp",EDGE,"E175"),sQuery(id+"F0.wireOp",EDGE,"E176"),sQuery(id+"F0.wireOp",EDGE,"E177"),sQuery(id+"F0.wireOp",EDGE,"E178"),sQuery(id+"F0.wireOp",EDGE,"E179"),sQuery(id+"F0.wireOp",EDGE,"E180"),sQuery(id+"F0.wireOp",EDGE,"E181"),sQuery(id+"F0.wireOp",EDGE,"E182"),sQuery(id+"F0.wireOp",EDGE,"E183"),sQuery(id+"F0.wireOp",EDGE,"E184"),sQuery(id+"F0.wireOp",EDGE,"E185"),sQuery(id+"F0.wireOp",EDGE,"E186"),sQuery(id+"F0.wireOp",EDGE,"E187"),sQuery(id+"F0.wireOp",EDGE,"E188"),sQuery(id+"F0.wireOp",EDGE,"E189"),sQuery(id+"F0.wireOp",EDGE,"E190"),sQuery(id+"F0.wireOp",EDGE,"E191"),sQuery(id+"F0.wireOp",EDGE,"E192"),sQuery(id+"F0.wireOp",EDGE,"E193"),sQuery(id+"F0.wireOp",EDGE,"E194"),sQuery(id+"F0.wireOp",EDGE,"E195"),sQuery(id+"F0.wireOp",EDGE,"E196"),sQuery(id+"F0.wireOp",EDGE,"E197"),sQuery(id+"F0.wireOp",EDGE,"E198"),sQuery(id+"F0.wireOp",EDGE,"E199"),sQuery(id+"F0.wireOp",EDGE,"E200"),sQuery(id+"F0.wireOp",EDGE,"E201"),sQuery(id+"F0.wireOp",EDGE,"E202"),sQuery(id+"F0.wireOp",EDGE,"E203"),sQuery(id+"F0.wireOp",EDGE,"E204"),sQuery(id+"F0.wireOp",EDGE,"E205"),sQuery(id+"F0.wireOp",EDGE,"E206"),sQuery(id+"F0.wireOp",EDGE,"E207"),sQuery(id+"F0.wireOp",EDGE,"E208"),sQuery(id+"F0.wireOp",EDGE,"E209"),sQuery(id+"F0.wireOp",EDGE,"E210"),sQuery(id+"F0.wireOp",EDGE,"E211"),sQuery(id+"F0.wireOp",EDGE,"E212"),sQuery(id+"F0.wireOp",EDGE,"E213"),sQuery(id+"F0.wireOp",EDGE,"E214"),sQuery(id+"F0.wireOp",EDGE,"E215"),sQuery(id+"F0.wireOp",EDGE,"E216"),sQuery(id+"F0.wireOp",EDGE,"E217"),sQuery(id+"F0.wireOp",EDGE,"E218"),sQuery(id+"F0.wireOp",EDGE,"E219"),sQuery(id+"F0.wireOp",EDGE,"E220"),sQuery(id+"F0.wireOp",EDGE,"E221"),sQuery(id+"F0.wireOp",EDGE,"E222"),sQuery(id+"F0.wireOp",EDGE,"E223"),sQuery(id+"F0.wireOp",EDGE,"E224"),sQuery(id+"F0.wireOp",EDGE,"E225"),sQuery(id+"F0.wireOp",EDGE,"E226"),sQuery(id+"F0.wireOp",EDGE,"E227"),sQuery(id+"F0.wireOp",EDGE,"E228"),sQuery(id+"F0.wireOp",EDGE,"E229"),sQuery(id+"F0.wireOp",EDGE,"E230"),sQuery(id+"F0.wireOp",EDGE,"E231"),sQuery(id+"F0.wireOp",EDGE,"E232"),sQuery(id+"F0.wireOp",EDGE,"E233"),sQuery(id+"F0.wireOp",EDGE,"E234"),sQuery(id+"F0.wireOp",EDGE,"E235"),sQuery(id+"F0.wireOp",EDGE,"E236"),sQuery(id+"F0.wireOp",EDGE,"E237"),sQuery(id+"F0.wireOp",EDGE,"E238"),sQuery(id+"F0.wireOp",EDGE,"E239"),sQuery(id+"F0.wireOp",EDGE,"E240"),sQuery(id+"F0.wireOp",EDGE,"E241"),sQuery(id+"F0.wireOp",EDGE,"E242"),sQuery(id+"F0.wireOp",EDGE,"E243"),sQuery(id+"F0.wireOp",EDGE,"E244"),sQuery(id+"F0.wireOp",EDGE,"E245"),sQuery(id+"F0.wireOp",EDGE,"E246"),sQuery(id+"F0.wireOp",EDGE,"E247"),sQuery(id+"F0.wireOp",EDGE,"E248"),sQuery(id+"F0.wireOp",EDGE,"E249"),sQuery(id+"F0.wireOp",EDGE,"E250"),sQuery(id+"F0.wireOp",EDGE,"E251"),sQuery(id+"F0.wireOp",EDGE,"E252"),sQuery(id+"F0.wireOp",EDGE,"E253"),sQuery(id+"F0.wireOp",EDGE,"E254"),sQuery(id+"F0.wireOp",EDGE,"E255"),sQuery(id+"F0.wireOp",EDGE,"E256"),sQuery(id+"F0.wireOp",EDGE,"E257"),sQuery(id+"F0.wireOp",EDGE,"E258"),sQuery(id+"F0.wireOp",EDGE,"E259"),sQuery(id+"F0.wireOp",EDGE,"E260"),sQuery(id+"F0.wireOp",EDGE,"E261"),sQuery(id+"F0.wireOp",EDGE,"E262"),sQuery(id+"F0.wireOp",EDGE,"E263"),sQuery(id+"F0.wireOp",EDGE,"E264"),sQuery(id+"F0.wireOp",EDGE,"E265"),sQuery(id+"F0.wireOp",EDGE,"E266"),sQuery(id+"F0.wireOp",EDGE,"E267"),sQuery(id+"F0.wireOp",EDGE,"E268"),sQuery(id+"F0.wireOp",EDGE,"E269"),sQuery(id+"F0.wireOp",EDGE,"E270"),sQuery(id+"F0.wireOp",EDGE,"E271"),sQuery(id+"F0.wireOp",EDGE,"E272"),sQuery(id+"F0.wireOp",EDGE,"E273"),sQuery(id+"F0.wireOp",EDGE,"E274"),sQuery(id+"F0.wireOp",EDGE,"E275"),sQuery(id+"F0.wireOp",EDGE,"E276"),sQuery(id+"F0.wireOp",EDGE,"E277"),sQuery(id+"F0.wireOp",EDGE,"E278"),sQuery(id+"F0.wireOp",EDGE,"E279"),sQuery(id+"F0.wireOp",EDGE,"E280"),sQuery(id+"F0.wireOp",EDGE,"E281"),sQuery(id+"F0.wireOp",EDGE,"E282"),sQuery(id+"F0.wireOp",EDGE,"E283"),sQuery(id+"F0.wireOp",EDGE,"E284"),sQuery(id+"F0.wireOp",EDGE,"E285"),sQuery(id+"F0.wireOp",EDGE,"E286"),sQuery(id+"F0.wireOp",EDGE,"E287"),sQuery(id+"F0.wireOp",EDGE,"E288"),sQuery(id+"F0.wireOp",EDGE,"E289"),sQuery(id+"F0.wireOp",EDGE,"E290"),sQuery(id+"F0.wireOp",EDGE,"E291"),sQuery(id+"F0.wireOp",EDGE,"E292"),sQuery(id+"F0.wireOp",EDGE,"E293"),sQuery(id+"F0.wireOp",EDGE,"E294"),sQuery(id+"F0.wireOp",EDGE,"E295"),sQuery(id+"F0.wireOp",EDGE,"E296"),sQuery(id+"F0.wireOp",EDGE,"E297"),sQuery(id+"F0.wireOp",EDGE,"E298"),sQuery(id+"F0.wireOp",EDGE,"E299"),sQuery(id+"F0.wireOp",EDGE,"E300"),sQuery(id+"F0.wireOp",EDGE,"E301"),sQuery(id+"F0.wireOp",EDGE,"E302"),sQuery(id+"F0.wireOp",EDGE,"E303"),sQuery(id+"F0.wireOp",EDGE,"E304"),sQuery(id+"F0.wireOp",EDGE,"E305"),sQuery(id+"F0.wireOp",EDGE,"E306"),sQuery(id+"F0.wireOp",EDGE,"E307"),sQuery(id+"F0.wireOp",EDGE,"E308"),sQuery(id+"F0.wireOp",EDGE,"E309"),sQuery(id+"F0.wireOp",EDGE,"E310"),sQuery(id+"F0.wireOp",EDGE,"E311"),sQuery(id+"F0.wireOp",EDGE,"E312"),sQuery(id+"F0.wireOp",EDGE,"E313"),sQuery(id+"F0.wireOp",EDGE,"E314"),sQuery(id+"F0.wireOp",EDGE,"E315"),sQuery(id+"F0.wireOp",EDGE,"E316"),sQuery(id+"F0.wireOp",EDGE,"E317"),sQuery(id+"F0.wireOp",EDGE,"E318"),sQuery(id+"F0.wireOp",EDGE,"E319"),sQuery(id+"F0.wireOp",EDGE,"E320"),sQuery(id+"F0.wireOp",EDGE,"E321"),sQuery(id+"F0.wireOp",EDGE,"E322"),sQuery(id+"F0.wireOp",EDGE,"E323"),sQuery(id+"F0.wireOp",EDGE,"E324"),sQuery(id+"F0.wireOp",EDGE,"E325"),sQuery(id+"F0.wireOp",EDGE,"E326"),sQuery(id+"F0.wireOp",EDGE,"E327"),sQuery(id+"F0.wireOp",EDGE,"E328"),sQuery(id+"F0.wireOp",EDGE,"E329"),sQuery(id+"F0.wireOp",EDGE,"E330"),sQuery(id+"F0.wireOp",EDGE,"E331"),sQuery(id+"F0.wireOp",EDGE,"E332"),sQuery(id+"F0.wireOp",EDGE,"E333"),sQuery(id+"F0.wireOp",EDGE,"E334"),sQuery(id+"F0.wireOp",EDGE,"E335"),sQuery(id+"F0.wireOp",EDGE,"E336"),sQuery(id+"F0.wireOp",EDGE,"E337"),sQuery(id+"F0.wireOp",EDGE,"E338"),sQuery(id+"F0.wireOp",EDGE,"E339"),sQuery(id+"F0.wireOp",EDGE,"E340"),sQuery(id+"F0.wireOp",EDGE,"E341"),sQuery(id+"F0.wireOp",EDGE,"E342"),sQuery(id+"F0.wireOp",EDGE,"E343"),sQuery(id+"F0.wireOp",EDGE,"E344"),sQuery(id+"F0.wireOp",EDGE,"E345"),sQuery(id+"F0.wireOp",EDGE,"E346"),sQuery(id+"F0.wireOp",EDGE,"E347"),sQuery(id+"F0.wireOp",EDGE,"E348"),sQuery(id+"F0.wireOp",EDGE,"E349"),sQuery(id+"F0.wireOp",EDGE,"E350"),sQuery(id+"F0.wireOp",EDGE,"E351"),sQuery(id+"F0.wireOp",EDGE,"E352"),sQuery(id+"F0.wireOp",EDGE,"E353"),sQuery(id+"F0.wireOp",EDGE,"E354"),sQuery(id+"F0.wireOp",EDGE,"E355"),sQuery(id+"F0.wireOp",EDGE,"E356"),sQuery(id+"F0.wireOp",EDGE,"E359"),sQuery(id+"F0.wireOp",EDGE,"E360"),sQuery(id+"F0.wireOp",EDGE,"E361"),sQuery(id+"F0.wireOp",EDGE,"E362"),sQuery(id+"F0.wireOp",EDGE,"E363"),sQuery(id+"F0.wireOp",EDGE,"E364"),sQuery(id+"F0.wireOp",EDGE,"E368"),sQuery(id+"F0.wireOp",EDGE,"E370"),sQuery(id+"F0.wireOp",EDGE,"E374"),sQuery(id+"F0.wireOp",EDGE,"E408"),sQuery(id+"F0.wireOp",EDGE,"E409"),sQuery(id+"F0.wireOp",EDGE,"E410"),sQuery(id+"F0.wireOp",EDGE,"E411"),sQuery(id+"F0.wireOp",EDGE,"E412"),sQuery(id+"F0.wireOp",EDGE,"E413"),sQuery(id+"F0.wireOp",EDGE,"E414"),sQuery(id+"F0.wireOp",EDGE,"E415"),sQuery(id+"F0.wireOp",EDGE,"E416"),sQuery(id+"F0.wireOp",EDGE,"E417"),sQuery(id+"F0.wireOp",EDGE,"E418"),sQuery(id+"F0.wireOp",EDGE,"E419"),sQuery(id+"F0.wireOp",EDGE,"E420"),sQuery(id+"F0.wireOp",EDGE,"E421"),sQuery(id+"F0.wireOp",EDGE,"E422"),sQuery(id+"F0.wireOp",EDGE,"E423"),sQuery(id+"F0.wireOp",EDGE,"E424"),sQuery(id+"F0.wireOp",EDGE,"E425"),sQuery(id+"F0.wireOp",EDGE,"E426"),sQuery(id+"F0.wireOp",EDGE,"E427"),sQuery(id+"F0.wireOp",EDGE,"E428"),sQuery(id+"F0.wireOp",EDGE,"E429"),sQuery(id+"F0.wireOp",EDGE,"E430"),sQuery(id+"F0.wireOp",EDGE,"E431"),sQuery(id+"F0.wireOp",EDGE,"E432"),sQuery(id+"F0.wireOp",EDGE,"E433"),sQuery(id+"F0.wireOp",EDGE,"E434"),sQuery(id+"F0.wireOp",EDGE,"E435"),sQuery(id+"F0.wireOp",EDGE,"E436"),sQuery(id+"F0.wireOp",EDGE,"E437"),sQuery(id+"F0.wireOp",EDGE,"E438"),sQuery(id+"F0.wireOp",EDGE,"E439"),sQuery(id+"F0.wireOp",EDGE,"E440"),sQuery(id+"F0.wireOp",EDGE,"E441"),sQuery(id+"F0.wireOp",EDGE,"E442"),sQuery(id+"F0.wireOp",EDGE,"E443"),sQuery(id+"F0.wireOp",EDGE,"E444"),sQuery(id+"F0.wireOp",EDGE,"E445"),sQuery(id+"F0.wireOp",EDGE,"E446"),sQuery(id+"F0.wireOp",EDGE,"E447"),sQuery(id+"F0.wireOp",EDGE,"E448"),sQuery(id+"F0.wireOp",EDGE,"E449"),sQuery(id+"F0.wireOp",EDGE,"E450"),sQuery(id+"F0.wireOp",EDGE,"E451"),sQuery(id+"F0.wireOp",EDGE,"E452"),sQuery(id+"F0.wireOp",EDGE,"E453"),sQuery(id+"F0.wireOp",EDGE,"E454"),sQuery(id+"F0.wireOp",EDGE,"E455"),sQuery(id+"F0.wireOp",EDGE,"E456"),sQuery(id+"F0.wireOp",EDGE,"E457"),sQuery(id+"F0.wireOp",EDGE,"E458"),sQuery(id+"F0.wireOp",EDGE,"E459"),sQuery(id+"F0.wireOp",EDGE,"E460"),sQuery(id+"F0.wireOp",EDGE,"E461"),sQuery(id+"F0.wireOp",EDGE,"E462"),sQuery(id+"F0.wireOp",EDGE,"E463"),sQuery(id+"F0.wireOp",EDGE,"E464"),sQuery(id+"F0.wireOp",EDGE,"E465"),sQuery(id+"F0.wireOp",EDGE,"E466"),sQuery(id+"F0.wireOp",EDGE,"E467"),sQuery(id+"F0.wireOp",EDGE,"E468"),sQuery(id+"F0.wireOp",EDGE,"E469"),sQuery(id+"F0.wireOp",EDGE,"E470"),sQuery(id+"F0.wireOp",EDGE,"E471"),sQuery(id+"F0.wireOp",EDGE,"E472"),sQuery(id+"F0.wireOp",EDGE,"E473"),sQuery(id+"F0.wireOp",EDGE,"E474"),sQuery(id+"F0.wireOp",EDGE,"E475"),sQuery(id+"F0.wireOp",EDGE,"E476"),sQuery(id+"F0.wireOp",EDGE,"E477"),sQuery(id+"F0.wireOp",EDGE,"E478"),sQuery(id+"F0.wireOp",EDGE,"E479"),sQuery(id+"F0.wireOp",EDGE,"E480"),sQuery(id+"F0.wireOp",EDGE,"E481"),sQuery(id+"F0.wireOp",EDGE,"E482"),sQuery(id+"F0.wireOp",EDGE,"E483"),sQuery(id+"F0.wireOp",EDGE,"E484"),sQuery(id+"F0.wireOp",EDGE,"E485"),sQuery(id+"F0.wireOp",EDGE,"E486"),sQuery(id+"F0.wireOp",EDGE,"E487"),sQuery(id+"F0.wireOp",EDGE,"E488"),sQuery(id+"F0.wireOp",EDGE,"E489"),sQuery(id+"F0.wireOp",EDGE,"E490"),sQuery(id+"F0.wireOp",EDGE,"E491"),sQuery(id+"F0.wireOp",EDGE,"E492"),sQuery(id+"F0.wireOp",EDGE,"E493"),sQuery(id+"F0.wireOp",EDGE,"E494"),sQuery(id+"F0.wireOp",EDGE,"E495"),sQuery(id+"F0.wireOp",EDGE,"E496"),sQuery(id+"F0.wireOp",EDGE,"E497"),sQuery(id+"F0.wireOp",EDGE,"E498"),sQuery(id+"F0.wireOp",EDGE,"E499"),sQuery(id+"F0.wireOp",EDGE,"E500"),sQuery(id+"F0.wireOp",EDGE,"E501"),sQuery(id+"F0.wireOp",EDGE,"E502"),sQuery(id+"F0.wireOp",EDGE,"E503"),sQuery(id+"F0.wireOp",EDGE,"E504"),sQuery(id+"F0.wireOp",EDGE,"E505"),sQuery(id+"F0.wireOp",EDGE,"E506"),sQuery(id+"F0.wireOp",EDGE,"E507"),sQuery(id+"F0.wireOp",EDGE,"E508"),sQuery(id+"F0.wireOp",EDGE,"E509"),sQuery(id+"F0.wireOp",EDGE,"E510"),sQuery(id+"F0.wireOp",EDGE,"E511"),sQuery(id+"F0.wireOp",EDGE,"E512"),sQuery(id+"F0.wireOp",EDGE,"E513"),sQuery(id+"F0.wireOp",EDGE,"E514"),sQuery(id+"F0.wireOp",EDGE,"E515"),sQuery(id+"F0.wireOp",EDGE,"E516"),sQuery(id+"F0.wireOp",EDGE,"E517"),sQuery(id+"F0.wireOp",EDGE,"E518"),sQuery(id+"F0.wireOp",EDGE,"E519"),sQuery(id+"F0.wireOp",EDGE,"E520"),sQuery(id+"F0.wireOp",EDGE,"E521"),sQuery(id+"F0.wireOp",EDGE,"E522"),sQuery(id+"F0.wireOp",EDGE,"E523"),sQuery(id+"F0.wireOp",EDGE,"E524"),sQuery(id+"F0.wireOp",EDGE,"E525"),sQuery(id+"F0.wireOp",EDGE,"E526"),sQuery(id+"F0.wireOp",EDGE,"E527"),sQuery(id+"F0.wireOp",EDGE,"E528"),sQuery(id+"F0.wireOp",EDGE,"E529"),sQuery(id+"F0.wireOp",EDGE,"E530"),sQuery(id+"F0.wireOp",EDGE,"E531"),sQuery(id+"F0.wireOp",EDGE,"E532"),sQuery(id+"F0.wireOp",EDGE,"E533"),sQuery(id+"F0.wireOp",EDGE,"E534"),sQuery(id+"F0.wireOp",EDGE,"E535"),sQuery(id+"F0.wireOp",EDGE,"E536"),sQuery(id+"F0.wireOp",EDGE,"E537"),sQuery(id+"F0.wireOp",EDGE,"E538"),sQuery(id+"F0.wireOp",EDGE,"E539"),sQuery(id+"F0.wireOp",EDGE,"E540"),sQuery(id+"F0.wireOp",EDGE,"E541"),sQuery(id+"F0.wireOp",EDGE,"E542"),sQuery(id+"F0.wireOp",EDGE,"E543"),sQuery(id+"F0.wireOp",EDGE,"E544"),sQuery(id+"F0.wireOp",EDGE,"E545"),sQuery(id+"F0.wireOp",EDGE,"E546"),sQuery(id+"F0.wireOp",EDGE,"E547"),sQuery(id+"F0.wireOp",EDGE,"E548"),sQuery(id+"F0.wireOp",EDGE,"E549"),sQuery(id+"F0.wireOp",EDGE,"E550"),sQuery(id+"F0.wireOp",EDGE,"E551"),sQuery(id+"F0.wireOp",EDGE,"E552"),sQuery(id+"F0.wireOp",EDGE,"E553"),sQuery(id+"F0.wireOp",EDGE,"E554"),sQuery(id+"F0.wireOp",EDGE,"E555"),sQuery(id+"F0.wireOp",EDGE,"E556"),sQuery(id+"F0.wireOp",EDGE,"E557"),sQuery(id+"F0.wireOp",EDGE,"E558"),sQuery(id+"F0.wireOp",EDGE,"E559"),sQuery(id+"F0.wireOp",EDGE,"E560"),sQuery(id+"F0.wireOp",EDGE,"E561"),sQuery(id+"F0.wireOp",EDGE,"E562"),sQuery(id+"F0.wireOp",EDGE,"E563"),sQuery(id+"F0.wireOp",EDGE,"E564"),sQuery(id+"F0.wireOp",EDGE,"E565"),sQuery(id+"F0.wireOp",EDGE,"E566"),sQuery(id+"F0.wireOp",EDGE,"E567"),sQuery(id+"F0.wireOp",EDGE,"E568"),sQuery(id+"F0.wireOp",EDGE,"E569"),sQuery(id+"F0.wireOp",EDGE,"E570"),sQuery(id+"F0.wireOp",EDGE,"E571"),sQuery(id+"F0.wireOp",EDGE,"E572"),sQuery(id+"F0.wireOp",EDGE,"E573"),sQuery(id+"F0.wireOp",EDGE,"E574"),sQuery(id+"F0.wireOp",EDGE,"E575"),sQuery(id+"F0.wireOp",EDGE,"E576"),sQuery(id+"F0.wireOp",EDGE,"E577"),sQuery(id+"F0.wireOp",EDGE,"E578"),sQuery(id+"F0.wireOp",EDGE,"E579"),sQuery(id+"F0.wireOp",EDGE,"E580"),sQuery(id+"F0.wireOp",EDGE,"E581"),sQuery(id+"F0.wireOp",EDGE,"E582"),sQuery(id+"F0.wireOp",EDGE,"E583"),sQuery(id+"F0.wireOp",EDGE,"E584"),sQuery(id+"F0.wireOp",EDGE,"E585"),sQuery(id+"F0.wireOp",EDGE,"E586"),sQuery(id+"F0.wireOp",EDGE,"E587"),sQuery(id+"F0.wireOp",EDGE,"E588"),sQuery(id+"F0.wireOp",EDGE,"E589"),sQuery(id+"F0.wireOp",EDGE,"E590"),sQuery(id+"F0.wireOp",EDGE,"E591"),sQuery(id+"F0.wireOp",EDGE,"E592"),sQuery(id+"F0.wireOp",EDGE,"E597"),sQuery(id+"F0.wireOp",EDGE,"E599"),sQuery(id+"F0.wireOp",EDGE,"E600"),sQuery(id+"F0.wireOp",EDGE,"E601"),sQuery(id+"F0.wireOp",EDGE,"E604"),sQuery(id+"F0.wireOp",EDGE,"E605"),sQuery(id+"F0.wireOp",EDGE,"E606"),sQuery(id+"F0.wireOp",EDGE,"E607"),sQuery(id+"F0.wireOp",EDGE,"E608"),sQuery(id+"F0.wireOp",EDGE,"E609"),sQuery(id+"F0.wireOp",EDGE,"E612"),sQuery(id+"F0.wireOp",EDGE,"E614"),sQuery(id+"F0.wireOp",EDGE,"E615"),sQuery(id+"F0.wireOp",EDGE,"E616"),sQuery(id+"F0.wireOp",EDGE,"E617"),sQuery(id+"F0.wireOp",EDGE,"E618"),sQuery(id+"F0.wireOp",EDGE,"E619"),sQuery(id+"F0.wireOp",EDGE,"E620"),sQuery(id+"F0.wireOp",EDGE,"E621"),sQuery(id+"F0.wireOp",EDGE,"E622"),sQuery(id+"F0.wireOp",EDGE,"E623"),sQuery(id+"F0.wireOp",EDGE,"E624"),sQuery(id+"F0.wireOp",EDGE,"E625"),sQuery(id+"F0.wireOp",EDGE,"E626"),sQuery(id+"F0.wireOp",EDGE,"E627"),sQuery(id+"F0.wireOp",EDGE,"E628"),sQuery(id+"F0.wireOp",EDGE,"E629"),sQuery(id+"F0.wireOp",EDGE,"E630"),sQuery(id+"F0.wireOp",EDGE,"E635"),sQuery(id+"F0.wireOp",EDGE,"E636"),sQuery(id+"F0.wireOp",EDGE,"E638"),sQuery(id+"F0.wireOp",EDGE,"E639"),sQuery(id+"F0.wireOp",EDGE,"E640"),sQuery(id+"F0.wireOp",EDGE,"E641"),sQuery(id+"F0.wireOp",EDGE,"E642"),sQuery(id+"F0.wireOp",EDGE,"E643"),sQuery(id+"F0.wireOp",EDGE,"E644"),sQuery(id+"F0.wireOp",EDGE,"E645"),sQuery(id+"F0.wireOp",EDGE,"E646"),sQuery(id+"F0.wireOp",EDGE,"E653"),sQuery(id+"F0.wireOp",EDGE,"E654"),sQuery(id+"F0.wireOp",EDGE,"E655"),sQuery(id+"F0.wireOp",EDGE,"E656"),sQuery(id+"F0.wireOp",EDGE,"E657"),sQuery(id+"F0.wireOp",EDGE,"E658"),sQuery(id+"F0.wireOp",EDGE,"E659"),sQuery(id+"F0.wireOp",EDGE,"E660"),sQuery(id+"F0.wireOp",EDGE,"E661"),sQuery(id+"F0.wireOp",EDGE,"E662"),sQuery(id+"F0.wireOp",EDGE,"E663"),sQuery(id+"F0.wireOp",EDGE,"E664"),sQuery(id+"F0.wireOp",EDGE,"E665"),sQuery(id+"F0.wireOp",EDGE,"E666"),sQuery(id+"F0.wireOp",EDGE,"E667"),sQuery(id+"F0.wireOp",EDGE,"E668"),sQuery(id+"F0.wireOp",EDGE,"E669"),sQuery(id+"F0.wireOp",EDGE,"E670"),sQuery(id+"F0.wireOp",EDGE,"E671"),sQuery(id+"F0.wireOp",EDGE,"E672"),sQuery(id+"F0.wireOp",EDGE,"E673"),sQuery(id+"F0.wireOp",EDGE,"E674")])],"isStart":false});
            var sketch = newSketch(context, id + "F2", { "sketchPlane" : qUnion([Q0])});
            skLineSegment(sketch, "E677", {"start": v(-7.33, 0) * mm, "end": v(35.33, 0) * mm, "construction": true});
            skPoint(sketch, "E678", {"position": v(14, 0) * mm});
            skCircle(sketch, "E679", {"center": v(14, 0) * mm, "radius": 17.5 * mm});
            skSolve(sketch);
        }
        {
            var Q0;
            Q0=makeQuery(id+"F2.imprint","IMPRINT",FACE,{"disambiguationData":[TD([[makeQuery(id+"F2.imprint","IMPRINT",EDGE,{"derivedFrom":sQuery(id+"F2.wireOp",EDGE,"E679")}),1.0]])]});
            var Q1;
            Q1 = qConstructionFilter(qBodyType(qCreatedBy(id + "F2" ,EDGE), BodyType.WIRE), ConstructionObject.NO);
            extrude(context, id + "F3", {"entities" : qUnion([Q0]), "operationType" : NewBodyOperationType.ADD, "surfaceEntities" : qUnion([Q1]), "depth" : 3.5 * mm, "offsetDistance" : 25 * mm});
        }
        {
            var Q0;
            Q0=makeQuery(id+"F1.opExtrude","CAP_FACE",FACE,{"disambiguationData":[OSD([sQuery(id+"F0.wireOp",EDGE,"E2"),sQuery(id+"F0.wireOp",EDGE,"E8"),sQuery(id+"F0.wireOp",EDGE,"E10"),sQuery(id+"F0.wireOp",EDGE,"E21"),sQuery(id+"F0.wireOp",EDGE,"E22"),sQuery(id+"F0.wireOp",EDGE,"E27"),sQuery(id+"F0.wireOp",EDGE,"E28"),sQuery(id+"F0.wireOp",EDGE,"E29"),sQuery(id+"F0.wireOp",EDGE,"E30"),sQuery(id+"F0.wireOp",EDGE,"E31"),sQuery(id+"F0.wireOp",EDGE,"E32"),sQuery(id+"F0.wireOp",EDGE,"E33"),sQuery(id+"F0.wireOp",EDGE,"E34"),sQuery(id+"F0.wireOp",EDGE,"E35"),sQuery(id+"F0.wireOp",EDGE,"E36"),sQuery(id+"F0.wireOp",EDGE,"E37"),sQuery(id+"F0.wireOp",EDGE,"E38"),sQuery(id+"F0.wireOp",EDGE,"E39"),sQuery(id+"F0.wireOp",EDGE,"E40"),sQuery(id+"F0.wireOp",EDGE,"E41"),sQuery(id+"F0.wireOp",EDGE,"E42"),sQuery(id+"F0.wireOp",EDGE,"E43"),sQuery(id+"F0.wireOp",EDGE,"E44"),sQuery(id+"F0.wireOp",EDGE,"E45"),sQuery(id+"F0.wireOp",EDGE,"E46"),sQuery(id+"F0.wireOp",EDGE,"E47"),sQuery(id+"F0.wireOp",EDGE,"E48"),sQuery(id+"F0.wireOp",EDGE,"E49"),sQuery(id+"F0.wireOp",EDGE,"E50"),sQuery(id+"F0.wireOp",EDGE,"E51"),sQuery(id+"F0.wireOp",EDGE,"E52"),sQuery(id+"F0.wireOp",EDGE,"E53"),sQuery(id+"F0.wireOp",EDGE,"E54"),sQuery(id+"F0.wireOp",EDGE,"E55"),sQuery(id+"F0.wireOp",EDGE,"E56"),sQuery(id+"F0.wireOp",EDGE,"E57"),sQuery(id+"F0.wireOp",EDGE,"E58"),sQuery(id+"F0.wireOp",EDGE,"E59"),sQuery(id+"F0.wireOp",EDGE,"E60"),sQuery(id+"F0.wireOp",EDGE,"E61"),sQuery(id+"F0.wireOp",EDGE,"E62"),sQuery(id+"F0.wireOp",EDGE,"E63"),sQuery(id+"F0.wireOp",EDGE,"E64"),sQuery(id+"F0.wireOp",EDGE,"E65"),sQuery(id+"F0.wireOp",EDGE,"E66"),sQuery(id+"F0.wireOp",EDGE,"E83"),sQuery(id+"F0.wireOp",EDGE,"E84"),sQuery(id+"F0.wireOp",EDGE,"E85"),sQuery(id+"F0.wireOp",EDGE,"E86"),sQuery(id+"F0.wireOp",EDGE,"E87"),sQuery(id+"F0.wireOp",EDGE,"E88"),sQuery(id+"F0.wireOp",EDGE,"E89"),sQuery(id+"F0.wireOp",EDGE,"E90"),sQuery(id+"F0.wireOp",EDGE,"E91"),sQuery(id+"F0.wireOp",EDGE,"E92"),sQuery(id+"F0.wireOp",EDGE,"E93"),sQuery(id+"F0.wireOp",EDGE,"E94"),sQuery(id+"F0.wireOp",EDGE,"E95"),sQuery(id+"F0.wireOp",EDGE,"E96"),sQuery(id+"F0.wireOp",EDGE,"E97"),sQuery(id+"F0.wireOp",EDGE,"E98"),sQuery(id+"F0.wireOp",EDGE,"E99"),sQuery(id+"F0.wireOp",EDGE,"E100"),sQuery(id+"F0.wireOp",EDGE,"E101"),sQuery(id+"F0.wireOp",EDGE,"E102"),sQuery(id+"F0.wireOp",EDGE,"E103"),sQuery(id+"F0.wireOp",EDGE,"E104"),sQuery(id+"F0.wireOp",EDGE,"E105"),sQuery(id+"F0.wireOp",EDGE,"E106"),sQuery(id+"F0.wireOp",EDGE,"E107"),sQuery(id+"F0.wireOp",EDGE,"E108"),sQuery(id+"F0.wireOp",EDGE,"E109"),sQuery(id+"F0.wireOp",EDGE,"E116"),sQuery(id+"F0.wireOp",EDGE,"E117"),sQuery(id+"F0.wireOp",EDGE,"E119"),sQuery(id+"F0.wireOp",EDGE,"E120"),sQuery(id+"F0.wireOp",EDGE,"E122"),sQuery(id+"F0.wireOp",EDGE,"E123"),sQuery(id+"F0.wireOp",EDGE,"E124"),sQuery(id+"F0.wireOp",EDGE,"E125"),sQuery(id+"F0.wireOp",EDGE,"E126"),sQuery(id+"F0.wireOp",EDGE,"E127"),sQuery(id+"F0.wireOp",EDGE,"E128"),sQuery(id+"F0.wireOp",EDGE,"E129"),sQuery(id+"F0.wireOp",EDGE,"E130"),sQuery(id+"F0.wireOp",EDGE,"E131"),sQuery(id+"F0.wireOp",EDGE,"E132"),sQuery(id+"F0.wireOp",EDGE,"E133"),sQuery(id+"F0.wireOp",EDGE,"E134"),sQuery(id+"F0.wireOp",EDGE,"E135"),sQuery(id+"F0.wireOp",EDGE,"E136"),sQuery(id+"F0.wireOp",EDGE,"E137"),sQuery(id+"F0.wireOp",EDGE,"E138"),sQuery(id+"F0.wireOp",EDGE,"E139"),sQuery(id+"F0.wireOp",EDGE,"E140"),sQuery(id+"F0.wireOp",EDGE,"E141"),sQuery(id+"F0.wireOp",EDGE,"E142"),sQuery(id+"F0.wireOp",EDGE,"E143"),sQuery(id+"F0.wireOp",EDGE,"E144"),sQuery(id+"F0.wireOp",EDGE,"E145"),sQuery(id+"F0.wireOp",EDGE,"E146"),sQuery(id+"F0.wireOp",EDGE,"E147"),sQuery(id+"F0.wireOp",EDGE,"E148"),sQuery(id+"F0.wireOp",EDGE,"E149"),sQuery(id+"F0.wireOp",EDGE,"E150"),sQuery(id+"F0.wireOp",EDGE,"E151"),sQuery(id+"F0.wireOp",EDGE,"E152"),sQuery(id+"F0.wireOp",EDGE,"E153"),sQuery(id+"F0.wireOp",EDGE,"E154"),sQuery(id+"F0.wireOp",EDGE,"E155"),sQuery(id+"F0.wireOp",EDGE,"E156"),sQuery(id+"F0.wireOp",EDGE,"E157"),sQuery(id+"F0.wireOp",EDGE,"E158"),sQuery(id+"F0.wireOp",EDGE,"E159"),sQuery(id+"F0.wireOp",EDGE,"E160"),sQuery(id+"F0.wireOp",EDGE,"E161"),sQuery(id+"F0.wireOp",EDGE,"E162"),sQuery(id+"F0.wireOp",EDGE,"E163"),sQuery(id+"F0.wireOp",EDGE,"E164"),sQuery(id+"F0.wireOp",EDGE,"E165"),sQuery(id+"F0.wireOp",EDGE,"E166"),sQuery(id+"F0.wireOp",EDGE,"E167"),sQuery(id+"F0.wireOp",EDGE,"E168"),sQuery(id+"F0.wireOp",EDGE,"E169"),sQuery(id+"F0.wireOp",EDGE,"E170"),sQuery(id+"F0.wireOp",EDGE,"E171"),sQuery(id+"F0.wireOp",EDGE,"E172"),sQuery(id+"F0.wireOp",EDGE,"E173"),sQuery(id+"F0.wireOp",EDGE,"E174"),sQuery(id+"F0.wireOp",EDGE,"E175"),sQuery(id+"F0.wireOp",EDGE,"E176"),sQuery(id+"F0.wireOp",EDGE,"E177"),sQuery(id+"F0.wireOp",EDGE,"E178"),sQuery(id+"F0.wireOp",EDGE,"E179"),sQuery(id+"F0.wireOp",EDGE,"E180"),sQuery(id+"F0.wireOp",EDGE,"E181"),sQuery(id+"F0.wireOp",EDGE,"E182"),sQuery(id+"F0.wireOp",EDGE,"E183"),sQuery(id+"F0.wireOp",EDGE,"E184"),sQuery(id+"F0.wireOp",EDGE,"E185"),sQuery(id+"F0.wireOp",EDGE,"E186"),sQuery(id+"F0.wireOp",EDGE,"E187"),sQuery(id+"F0.wireOp",EDGE,"E188"),sQuery(id+"F0.wireOp",EDGE,"E189"),sQuery(id+"F0.wireOp",EDGE,"E190"),sQuery(id+"F0.wireOp",EDGE,"E191"),sQuery(id+"F0.wireOp",EDGE,"E192"),sQuery(id+"F0.wireOp",EDGE,"E193"),sQuery(id+"F0.wireOp",EDGE,"E194"),sQuery(id+"F0.wireOp",EDGE,"E195"),sQuery(id+"F0.wireOp",EDGE,"E196"),sQuery(id+"F0.wireOp",EDGE,"E197"),sQuery(id+"F0.wireOp",EDGE,"E198"),sQuery(id+"F0.wireOp",EDGE,"E199"),sQuery(id+"F0.wireOp",EDGE,"E200"),sQuery(id+"F0.wireOp",EDGE,"E201"),sQuery(id+"F0.wireOp",EDGE,"E202"),sQuery(id+"F0.wireOp",EDGE,"E203"),sQuery(id+"F0.wireOp",EDGE,"E204"),sQuery(id+"F0.wireOp",EDGE,"E205"),sQuery(id+"F0.wireOp",EDGE,"E206"),sQuery(id+"F0.wireOp",EDGE,"E207"),sQuery(id+"F0.wireOp",EDGE,"E208"),sQuery(id+"F0.wireOp",EDGE,"E209"),sQuery(id+"F0.wireOp",EDGE,"E210"),sQuery(id+"F0.wireOp",EDGE,"E211"),sQuery(id+"F0.wireOp",EDGE,"E212"),sQuery(id+"F0.wireOp",EDGE,"E213"),sQuery(id+"F0.wireOp",EDGE,"E214"),sQuery(id+"F0.wireOp",EDGE,"E215"),sQuery(id+"F0.wireOp",EDGE,"E216"),sQuery(id+"F0.wireOp",EDGE,"E217"),sQuery(id+"F0.wireOp",EDGE,"E218"),sQuery(id+"F0.wireOp",EDGE,"E219"),sQuery(id+"F0.wireOp",EDGE,"E220"),sQuery(id+"F0.wireOp",EDGE,"E221"),sQuery(id+"F0.wireOp",EDGE,"E222"),sQuery(id+"F0.wireOp",EDGE,"E223"),sQuery(id+"F0.wireOp",EDGE,"E224"),sQuery(id+"F0.wireOp",EDGE,"E225"),sQuery(id+"F0.wireOp",EDGE,"E226"),sQuery(id+"F0.wireOp",EDGE,"E227"),sQuery(id+"F0.wireOp",EDGE,"E228"),sQuery(id+"F0.wireOp",EDGE,"E229"),sQuery(id+"F0.wireOp",EDGE,"E230"),sQuery(id+"F0.wireOp",EDGE,"E231"),sQuery(id+"F0.wireOp",EDGE,"E232"),sQuery(id+"F0.wireOp",EDGE,"E233"),sQuery(id+"F0.wireOp",EDGE,"E234"),sQuery(id+"F0.wireOp",EDGE,"E235"),sQuery(id+"F0.wireOp",EDGE,"E236"),sQuery(id+"F0.wireOp",EDGE,"E237"),sQuery(id+"F0.wireOp",EDGE,"E238"),sQuery(id+"F0.wireOp",EDGE,"E239"),sQuery(id+"F0.wireOp",EDGE,"E240"),sQuery(id+"F0.wireOp",EDGE,"E241"),sQuery(id+"F0.wireOp",EDGE,"E242"),sQuery(id+"F0.wireOp",EDGE,"E243"),sQuery(id+"F0.wireOp",EDGE,"E244"),sQuery(id+"F0.wireOp",EDGE,"E245"),sQuery(id+"F0.wireOp",EDGE,"E246"),sQuery(id+"F0.wireOp",EDGE,"E247"),sQuery(id+"F0.wireOp",EDGE,"E248"),sQuery(id+"F0.wireOp",EDGE,"E249"),sQuery(id+"F0.wireOp",EDGE,"E250"),sQuery(id+"F0.wireOp",EDGE,"E251"),sQuery(id+"F0.wireOp",EDGE,"E252"),sQuery(id+"F0.wireOp",EDGE,"E253"),sQuery(id+"F0.wireOp",EDGE,"E254"),sQuery(id+"F0.wireOp",EDGE,"E255"),sQuery(id+"F0.wireOp",EDGE,"E256"),sQuery(id+"F0.wireOp",EDGE,"E257"),sQuery(id+"F0.wireOp",EDGE,"E258"),sQuery(id+"F0.wireOp",EDGE,"E259"),sQuery(id+"F0.wireOp",EDGE,"E260"),sQuery(id+"F0.wireOp",EDGE,"E261"),sQuery(id+"F0.wireOp",EDGE,"E262"),sQuery(id+"F0.wireOp",EDGE,"E263"),sQuery(id+"F0.wireOp",EDGE,"E264"),sQuery(id+"F0.wireOp",EDGE,"E265"),sQuery(id+"F0.wireOp",EDGE,"E266"),sQuery(id+"F0.wireOp",EDGE,"E267"),sQuery(id+"F0.wireOp",EDGE,"E268"),sQuery(id+"F0.wireOp",EDGE,"E269"),sQuery(id+"F0.wireOp",EDGE,"E270"),sQuery(id+"F0.wireOp",EDGE,"E271"),sQuery(id+"F0.wireOp",EDGE,"E272"),sQuery(id+"F0.wireOp",EDGE,"E273"),sQuery(id+"F0.wireOp",EDGE,"E274"),sQuery(id+"F0.wireOp",EDGE,"E275"),sQuery(id+"F0.wireOp",EDGE,"E276"),sQuery(id+"F0.wireOp",EDGE,"E277"),sQuery(id+"F0.wireOp",EDGE,"E278"),sQuery(id+"F0.wireOp",EDGE,"E279"),sQuery(id+"F0.wireOp",EDGE,"E280"),sQuery(id+"F0.wireOp",EDGE,"E281"),sQuery(id+"F0.wireOp",EDGE,"E282"),sQuery(id+"F0.wireOp",EDGE,"E283"),sQuery(id+"F0.wireOp",EDGE,"E284"),sQuery(id+"F0.wireOp",EDGE,"E285"),sQuery(id+"F0.wireOp",EDGE,"E286"),sQuery(id+"F0.wireOp",EDGE,"E287"),sQuery(id+"F0.wireOp",EDGE,"E288"),sQuery(id+"F0.wireOp",EDGE,"E289"),sQuery(id+"F0.wireOp",EDGE,"E290"),sQuery(id+"F0.wireOp",EDGE,"E291"),sQuery(id+"F0.wireOp",EDGE,"E292"),sQuery(id+"F0.wireOp",EDGE,"E293"),sQuery(id+"F0.wireOp",EDGE,"E294"),sQuery(id+"F0.wireOp",EDGE,"E295"),sQuery(id+"F0.wireOp",EDGE,"E296"),sQuery(id+"F0.wireOp",EDGE,"E297"),sQuery(id+"F0.wireOp",EDGE,"E298"),sQuery(id+"F0.wireOp",EDGE,"E299"),sQuery(id+"F0.wireOp",EDGE,"E300"),sQuery(id+"F0.wireOp",EDGE,"E301"),sQuery(id+"F0.wireOp",EDGE,"E302"),sQuery(id+"F0.wireOp",EDGE,"E303"),sQuery(id+"F0.wireOp",EDGE,"E304"),sQuery(id+"F0.wireOp",EDGE,"E305"),sQuery(id+"F0.wireOp",EDGE,"E306"),sQuery(id+"F0.wireOp",EDGE,"E307"),sQuery(id+"F0.wireOp",EDGE,"E308"),sQuery(id+"F0.wireOp",EDGE,"E309"),sQuery(id+"F0.wireOp",EDGE,"E310"),sQuery(id+"F0.wireOp",EDGE,"E311"),sQuery(id+"F0.wireOp",EDGE,"E312"),sQuery(id+"F0.wireOp",EDGE,"E313"),sQuery(id+"F0.wireOp",EDGE,"E314"),sQuery(id+"F0.wireOp",EDGE,"E315"),sQuery(id+"F0.wireOp",EDGE,"E316"),sQuery(id+"F0.wireOp",EDGE,"E317"),sQuery(id+"F0.wireOp",EDGE,"E318"),sQuery(id+"F0.wireOp",EDGE,"E319"),sQuery(id+"F0.wireOp",EDGE,"E320"),sQuery(id+"F0.wireOp",EDGE,"E321"),sQuery(id+"F0.wireOp",EDGE,"E322"),sQuery(id+"F0.wireOp",EDGE,"E323"),sQuery(id+"F0.wireOp",EDGE,"E324"),sQuery(id+"F0.wireOp",EDGE,"E325"),sQuery(id+"F0.wireOp",EDGE,"E326"),sQuery(id+"F0.wireOp",EDGE,"E327"),sQuery(id+"F0.wireOp",EDGE,"E328"),sQuery(id+"F0.wireOp",EDGE,"E329"),sQuery(id+"F0.wireOp",EDGE,"E330"),sQuery(id+"F0.wireOp",EDGE,"E331"),sQuery(id+"F0.wireOp",EDGE,"E332"),sQuery(id+"F0.wireOp",EDGE,"E333"),sQuery(id+"F0.wireOp",EDGE,"E334"),sQuery(id+"F0.wireOp",EDGE,"E335"),sQuery(id+"F0.wireOp",EDGE,"E336"),sQuery(id+"F0.wireOp",EDGE,"E337"),sQuery(id+"F0.wireOp",EDGE,"E338"),sQuery(id+"F0.wireOp",EDGE,"E339"),sQuery(id+"F0.wireOp",EDGE,"E340"),sQuery(id+"F0.wireOp",EDGE,"E341"),sQuery(id+"F0.wireOp",EDGE,"E342"),sQuery(id+"F0.wireOp",EDGE,"E343"),sQuery(id+"F0.wireOp",EDGE,"E344"),sQuery(id+"F0.wireOp",EDGE,"E345"),sQuery(id+"F0.wireOp",EDGE,"E346"),sQuery(id+"F0.wireOp",EDGE,"E347"),sQuery(id+"F0.wireOp",EDGE,"E348"),sQuery(id+"F0.wireOp",EDGE,"E349"),sQuery(id+"F0.wireOp",EDGE,"E350"),sQuery(id+"F0.wireOp",EDGE,"E351"),sQuery(id+"F0.wireOp",EDGE,"E352"),sQuery(id+"F0.wireOp",EDGE,"E353"),sQuery(id+"F0.wireOp",EDGE,"E354"),sQuery(id+"F0.wireOp",EDGE,"E355"),sQuery(id+"F0.wireOp",EDGE,"E356"),sQuery(id+"F0.wireOp",EDGE,"E359"),sQuery(id+"F0.wireOp",EDGE,"E360"),sQuery(id+"F0.wireOp",EDGE,"E361"),sQuery(id+"F0.wireOp",EDGE,"E362"),sQuery(id+"F0.wireOp",EDGE,"E363"),sQuery(id+"F0.wireOp",EDGE,"E364"),sQuery(id+"F0.wireOp",EDGE,"E368"),sQuery(id+"F0.wireOp",EDGE,"E370"),sQuery(id+"F0.wireOp",EDGE,"E374"),sQuery(id+"F0.wireOp",EDGE,"E408"),sQuery(id+"F0.wireOp",EDGE,"E409"),sQuery(id+"F0.wireOp",EDGE,"E410"),sQuery(id+"F0.wireOp",EDGE,"E411"),sQuery(id+"F0.wireOp",EDGE,"E412"),sQuery(id+"F0.wireOp",EDGE,"E413"),sQuery(id+"F0.wireOp",EDGE,"E414"),sQuery(id+"F0.wireOp",EDGE,"E415"),sQuery(id+"F0.wireOp",EDGE,"E416"),sQuery(id+"F0.wireOp",EDGE,"E417"),sQuery(id+"F0.wireOp",EDGE,"E418"),sQuery(id+"F0.wireOp",EDGE,"E419"),sQuery(id+"F0.wireOp",EDGE,"E420"),sQuery(id+"F0.wireOp",EDGE,"E421"),sQuery(id+"F0.wireOp",EDGE,"E422"),sQuery(id+"F0.wireOp",EDGE,"E423"),sQuery(id+"F0.wireOp",EDGE,"E424"),sQuery(id+"F0.wireOp",EDGE,"E425"),sQuery(id+"F0.wireOp",EDGE,"E426"),sQuery(id+"F0.wireOp",EDGE,"E427"),sQuery(id+"F0.wireOp",EDGE,"E428"),sQuery(id+"F0.wireOp",EDGE,"E429"),sQuery(id+"F0.wireOp",EDGE,"E430"),sQuery(id+"F0.wireOp",EDGE,"E431"),sQuery(id+"F0.wireOp",EDGE,"E432"),sQuery(id+"F0.wireOp",EDGE,"E433"),sQuery(id+"F0.wireOp",EDGE,"E434"),sQuery(id+"F0.wireOp",EDGE,"E435"),sQuery(id+"F0.wireOp",EDGE,"E436"),sQuery(id+"F0.wireOp",EDGE,"E437"),sQuery(id+"F0.wireOp",EDGE,"E438"),sQuery(id+"F0.wireOp",EDGE,"E439"),sQuery(id+"F0.wireOp",EDGE,"E440"),sQuery(id+"F0.wireOp",EDGE,"E441"),sQuery(id+"F0.wireOp",EDGE,"E442"),sQuery(id+"F0.wireOp",EDGE,"E443"),sQuery(id+"F0.wireOp",EDGE,"E444"),sQuery(id+"F0.wireOp",EDGE,"E445"),sQuery(id+"F0.wireOp",EDGE,"E446"),sQuery(id+"F0.wireOp",EDGE,"E447"),sQuery(id+"F0.wireOp",EDGE,"E448"),sQuery(id+"F0.wireOp",EDGE,"E449"),sQuery(id+"F0.wireOp",EDGE,"E450"),sQuery(id+"F0.wireOp",EDGE,"E451"),sQuery(id+"F0.wireOp",EDGE,"E452"),sQuery(id+"F0.wireOp",EDGE,"E453"),sQuery(id+"F0.wireOp",EDGE,"E454"),sQuery(id+"F0.wireOp",EDGE,"E455"),sQuery(id+"F0.wireOp",EDGE,"E456"),sQuery(id+"F0.wireOp",EDGE,"E457"),sQuery(id+"F0.wireOp",EDGE,"E458"),sQuery(id+"F0.wireOp",EDGE,"E459"),sQuery(id+"F0.wireOp",EDGE,"E460"),sQuery(id+"F0.wireOp",EDGE,"E461"),sQuery(id+"F0.wireOp",EDGE,"E462"),sQuery(id+"F0.wireOp",EDGE,"E463"),sQuery(id+"F0.wireOp",EDGE,"E464"),sQuery(id+"F0.wireOp",EDGE,"E465"),sQuery(id+"F0.wireOp",EDGE,"E466"),sQuery(id+"F0.wireOp",EDGE,"E467"),sQuery(id+"F0.wireOp",EDGE,"E468"),sQuery(id+"F0.wireOp",EDGE,"E469"),sQuery(id+"F0.wireOp",EDGE,"E470"),sQuery(id+"F0.wireOp",EDGE,"E471"),sQuery(id+"F0.wireOp",EDGE,"E472"),sQuery(id+"F0.wireOp",EDGE,"E473"),sQuery(id+"F0.wireOp",EDGE,"E474"),sQuery(id+"F0.wireOp",EDGE,"E475"),sQuery(id+"F0.wireOp",EDGE,"E476"),sQuery(id+"F0.wireOp",EDGE,"E477"),sQuery(id+"F0.wireOp",EDGE,"E478"),sQuery(id+"F0.wireOp",EDGE,"E479"),sQuery(id+"F0.wireOp",EDGE,"E480"),sQuery(id+"F0.wireOp",EDGE,"E481"),sQuery(id+"F0.wireOp",EDGE,"E482"),sQuery(id+"F0.wireOp",EDGE,"E483"),sQuery(id+"F0.wireOp",EDGE,"E484"),sQuery(id+"F0.wireOp",EDGE,"E485"),sQuery(id+"F0.wireOp",EDGE,"E486"),sQuery(id+"F0.wireOp",EDGE,"E487"),sQuery(id+"F0.wireOp",EDGE,"E488"),sQuery(id+"F0.wireOp",EDGE,"E489"),sQuery(id+"F0.wireOp",EDGE,"E490"),sQuery(id+"F0.wireOp",EDGE,"E491"),sQuery(id+"F0.wireOp",EDGE,"E492"),sQuery(id+"F0.wireOp",EDGE,"E493"),sQuery(id+"F0.wireOp",EDGE,"E494"),sQuery(id+"F0.wireOp",EDGE,"E495"),sQuery(id+"F0.wireOp",EDGE,"E496"),sQuery(id+"F0.wireOp",EDGE,"E497"),sQuery(id+"F0.wireOp",EDGE,"E498"),sQuery(id+"F0.wireOp",EDGE,"E499"),sQuery(id+"F0.wireOp",EDGE,"E500"),sQuery(id+"F0.wireOp",EDGE,"E501"),sQuery(id+"F0.wireOp",EDGE,"E502"),sQuery(id+"F0.wireOp",EDGE,"E503"),sQuery(id+"F0.wireOp",EDGE,"E504"),sQuery(id+"F0.wireOp",EDGE,"E505"),sQuery(id+"F0.wireOp",EDGE,"E506"),sQuery(id+"F0.wireOp",EDGE,"E507"),sQuery(id+"F0.wireOp",EDGE,"E508"),sQuery(id+"F0.wireOp",EDGE,"E509"),sQuery(id+"F0.wireOp",EDGE,"E510"),sQuery(id+"F0.wireOp",EDGE,"E511"),sQuery(id+"F0.wireOp",EDGE,"E512"),sQuery(id+"F0.wireOp",EDGE,"E513"),sQuery(id+"F0.wireOp",EDGE,"E514"),sQuery(id+"F0.wireOp",EDGE,"E515"),sQuery(id+"F0.wireOp",EDGE,"E516"),sQuery(id+"F0.wireOp",EDGE,"E517"),sQuery(id+"F0.wireOp",EDGE,"E518"),sQuery(id+"F0.wireOp",EDGE,"E519"),sQuery(id+"F0.wireOp",EDGE,"E520"),sQuery(id+"F0.wireOp",EDGE,"E521"),sQuery(id+"F0.wireOp",EDGE,"E522"),sQuery(id+"F0.wireOp",EDGE,"E523"),sQuery(id+"F0.wireOp",EDGE,"E524"),sQuery(id+"F0.wireOp",EDGE,"E525"),sQuery(id+"F0.wireOp",EDGE,"E526"),sQuery(id+"F0.wireOp",EDGE,"E527"),sQuery(id+"F0.wireOp",EDGE,"E528"),sQuery(id+"F0.wireOp",EDGE,"E529"),sQuery(id+"F0.wireOp",EDGE,"E530"),sQuery(id+"F0.wireOp",EDGE,"E531"),sQuery(id+"F0.wireOp",EDGE,"E532"),sQuery(id+"F0.wireOp",EDGE,"E533"),sQuery(id+"F0.wireOp",EDGE,"E534"),sQuery(id+"F0.wireOp",EDGE,"E535"),sQuery(id+"F0.wireOp",EDGE,"E536"),sQuery(id+"F0.wireOp",EDGE,"E537"),sQuery(id+"F0.wireOp",EDGE,"E538"),sQuery(id+"F0.wireOp",EDGE,"E539"),sQuery(id+"F0.wireOp",EDGE,"E540"),sQuery(id+"F0.wireOp",EDGE,"E541"),sQuery(id+"F0.wireOp",EDGE,"E542"),sQuery(id+"F0.wireOp",EDGE,"E543"),sQuery(id+"F0.wireOp",EDGE,"E544"),sQuery(id+"F0.wireOp",EDGE,"E545"),sQuery(id+"F0.wireOp",EDGE,"E546"),sQuery(id+"F0.wireOp",EDGE,"E547"),sQuery(id+"F0.wireOp",EDGE,"E548"),sQuery(id+"F0.wireOp",EDGE,"E549"),sQuery(id+"F0.wireOp",EDGE,"E550"),sQuery(id+"F0.wireOp",EDGE,"E551"),sQuery(id+"F0.wireOp",EDGE,"E552"),sQuery(id+"F0.wireOp",EDGE,"E553"),sQuery(id+"F0.wireOp",EDGE,"E554"),sQuery(id+"F0.wireOp",EDGE,"E555"),sQuery(id+"F0.wireOp",EDGE,"E556"),sQuery(id+"F0.wireOp",EDGE,"E557"),sQuery(id+"F0.wireOp",EDGE,"E558"),sQuery(id+"F0.wireOp",EDGE,"E559"),sQuery(id+"F0.wireOp",EDGE,"E560"),sQuery(id+"F0.wireOp",EDGE,"E561"),sQuery(id+"F0.wireOp",EDGE,"E562"),sQuery(id+"F0.wireOp",EDGE,"E563"),sQuery(id+"F0.wireOp",EDGE,"E564"),sQuery(id+"F0.wireOp",EDGE,"E565"),sQuery(id+"F0.wireOp",EDGE,"E566"),sQuery(id+"F0.wireOp",EDGE,"E567"),sQuery(id+"F0.wireOp",EDGE,"E568"),sQuery(id+"F0.wireOp",EDGE,"E569"),sQuery(id+"F0.wireOp",EDGE,"E570"),sQuery(id+"F0.wireOp",EDGE,"E571"),sQuery(id+"F0.wireOp",EDGE,"E572"),sQuery(id+"F0.wireOp",EDGE,"E573"),sQuery(id+"F0.wireOp",EDGE,"E574"),sQuery(id+"F0.wireOp",EDGE,"E575"),sQuery(id+"F0.wireOp",EDGE,"E576"),sQuery(id+"F0.wireOp",EDGE,"E577"),sQuery(id+"F0.wireOp",EDGE,"E578"),sQuery(id+"F0.wireOp",EDGE,"E579"),sQuery(id+"F0.wireOp",EDGE,"E580"),sQuery(id+"F0.wireOp",EDGE,"E581"),sQuery(id+"F0.wireOp",EDGE,"E582"),sQuery(id+"F0.wireOp",EDGE,"E583"),sQuery(id+"F0.wireOp",EDGE,"E584"),sQuery(id+"F0.wireOp",EDGE,"E585"),sQuery(id+"F0.wireOp",EDGE,"E586"),sQuery(id+"F0.wireOp",EDGE,"E587"),sQuery(id+"F0.wireOp",EDGE,"E588"),sQuery(id+"F0.wireOp",EDGE,"E589"),sQuery(id+"F0.wireOp",EDGE,"E590"),sQuery(id+"F0.wireOp",EDGE,"E591"),sQuery(id+"F0.wireOp",EDGE,"E592"),sQuery(id+"F0.wireOp",EDGE,"E597"),sQuery(id+"F0.wireOp",EDGE,"E599"),sQuery(id+"F0.wireOp",EDGE,"E600"),sQuery(id+"F0.wireOp",EDGE,"E601"),sQuery(id+"F0.wireOp",EDGE,"E604"),sQuery(id+"F0.wireOp",EDGE,"E605"),sQuery(id+"F0.wireOp",EDGE,"E606"),sQuery(id+"F0.wireOp",EDGE,"E607"),sQuery(id+"F0.wireOp",EDGE,"E608"),sQuery(id+"F0.wireOp",EDGE,"E609"),sQuery(id+"F0.wireOp",EDGE,"E612"),sQuery(id+"F0.wireOp",EDGE,"E614"),sQuery(id+"F0.wireOp",EDGE,"E615"),sQuery(id+"F0.wireOp",EDGE,"E616"),sQuery(id+"F0.wireOp",EDGE,"E617"),sQuery(id+"F0.wireOp",EDGE,"E618"),sQuery(id+"F0.wireOp",EDGE,"E619"),sQuery(id+"F0.wireOp",EDGE,"E620"),sQuery(id+"F0.wireOp",EDGE,"E621"),sQuery(id+"F0.wireOp",EDGE,"E622"),sQuery(id+"F0.wireOp",EDGE,"E623"),sQuery(id+"F0.wireOp",EDGE,"E624"),sQuery(id+"F0.wireOp",EDGE,"E625"),sQuery(id+"F0.wireOp",EDGE,"E626"),sQuery(id+"F0.wireOp",EDGE,"E627"),sQuery(id+"F0.wireOp",EDGE,"E628"),sQuery(id+"F0.wireOp",EDGE,"E629"),sQuery(id+"F0.wireOp",EDGE,"E630"),sQuery(id+"F0.wireOp",EDGE,"E635"),sQuery(id+"F0.wireOp",EDGE,"E636"),sQuery(id+"F0.wireOp",EDGE,"E638"),sQuery(id+"F0.wireOp",EDGE,"E639"),sQuery(id+"F0.wireOp",EDGE,"E640"),sQuery(id+"F0.wireOp",EDGE,"E641"),sQuery(id+"F0.wireOp",EDGE,"E642"),sQuery(id+"F0.wireOp",EDGE,"E643"),sQuery(id+"F0.wireOp",EDGE,"E644"),sQuery(id+"F0.wireOp",EDGE,"E645"),sQuery(id+"F0.wireOp",EDGE,"E646"),sQuery(id+"F0.wireOp",EDGE,"E653"),sQuery(id+"F0.wireOp",EDGE,"E654"),sQuery(id+"F0.wireOp",EDGE,"E655"),sQuery(id+"F0.wireOp",EDGE,"E656"),sQuery(id+"F0.wireOp",EDGE,"E657"),sQuery(id+"F0.wireOp",EDGE,"E658"),sQuery(id+"F0.wireOp",EDGE,"E659"),sQuery(id+"F0.wireOp",EDGE,"E660"),sQuery(id+"F0.wireOp",EDGE,"E661"),sQuery(id+"F0.wireOp",EDGE,"E662"),sQuery(id+"F0.wireOp",EDGE,"E663"),sQuery(id+"F0.wireOp",EDGE,"E664"),sQuery(id+"F0.wireOp",EDGE,"E665"),sQuery(id+"F0.wireOp",EDGE,"E666"),sQuery(id+"F0.wireOp",EDGE,"E667"),sQuery(id+"F0.wireOp",EDGE,"E668"),sQuery(id+"F0.wireOp",EDGE,"E669"),sQuery(id+"F0.wireOp",EDGE,"E670"),sQuery(id+"F0.wireOp",EDGE,"E671"),sQuery(id+"F0.wireOp",EDGE,"E672"),sQuery(id+"F0.wireOp",EDGE,"E673"),sQuery(id+"F0.wireOp",EDGE,"E674")])],"isStart":true});
            var sketch = newSketch(context, id + "F4", { "sketchPlane" : qUnion([Q0])});
            skCircle(sketch, "E680", {"center": v(14, 0) * mm, "radius": 18.5 * mm});
            skLineSegment(sketch, "E681", {"start": v(35.33, 0) * mm, "end": v(-7.33, 0) * mm});
            skSolve(sketch);
        }
        {
            var Q0;
            Q0 = qSketchRegion(id + "F4", true);
            extrude(context, id + "F5", {"entities" : qUnion([Q0]), "operationType" : NewBodyOperationType.ADD, "depth" : 24.1 * mm, "offsetDistance" : 25 * mm});
        }
        {
            var Q0;
            Q0=makeQuery(id+"F5.opExtrude","CAP_FACE",FACE,{"disambiguationData":[OSD([sQuery(id+"F4.wireOp",EDGE,"E680")])],"isStart":false});
            var sketch = newSketch(context, id + "F6", { "sketchPlane" : qUnion([Q0])});
            skLineSegment(sketch, "E682", {"start": v(32.5, 0) * mm, "end": v(-4.5, 0) * mm, "construction": true});
            skLineSegment(sketch, "E683.bottom", {"start": v(0, -1.7) * mm, "end": v(28, -1.7) * mm});
            skLineSegment(sketch, "E683.top", {"start": v(0, 1.7) * mm, "end": v(28, 1.7) * mm});
            skLineSegment(sketch, "E683.left", {"start": v(0, -1.7) * mm, "end": v(0, 1.7) * mm});
            skLineSegment(sketch, "E683.right", {"start": v(28, -1.7) * mm, "end": v(28, 1.7) * mm});
            skPoint(sketch, "E683.middle", {"position": v(14, 0) * mm});
            skSolve(sketch);
        }
        {
            var Q0;
            Q0 = qSketchRegion(id + "F6", true);
            extrude(context, id + "F7", {"entities" : qUnion([Q0]), "operationType" : NewBodyOperationType.REMOVE, "oppositeDirection" : true, "depth" : 32 * mm, "offsetDistance" : 25 * mm});
        }
        {
            var Q0;
            Q0=makeQuery(id+"F3.opExtrude","CAP_FACE",FACE,{"disambiguationData":[OSD([sQuery(id+"F2.wireOp",EDGE,"E679")])],"isStart":false});
            var sketch = newSketch(context, id + "F8", { "sketchPlane" : qUnion([Q0])});
            skCircle(sketch, "E684", {"center": v(14, 10) * mm, "radius": 1 * mm});
            skCircle(sketch, "E685", {"center": v(14, -10) * mm, "radius": 1 * mm});
            skPoint(sketch, "E686.0", {"position": v(14, 1.7) * mm});
            skPoint(sketch, "E687.0", {"position": v(28, 0) * mm});
            skLineSegment(sketch, "E688", {"start": v(28, 0) * mm, "end": v(22.31, 0) * mm, "construction": true});
            skSolve(sketch);
        }
        {
            var Q0;
            Q0 = qSketchRegion(id + "F8", true);
            extrude(context, id + "F9", {"entities" : qUnion([Q0]), "operationType" : NewBodyOperationType.REMOVE, "oppositeDirection" : true, "depth" : 2 * mm, "offsetDistance" : 25 * mm});
        }
    });
